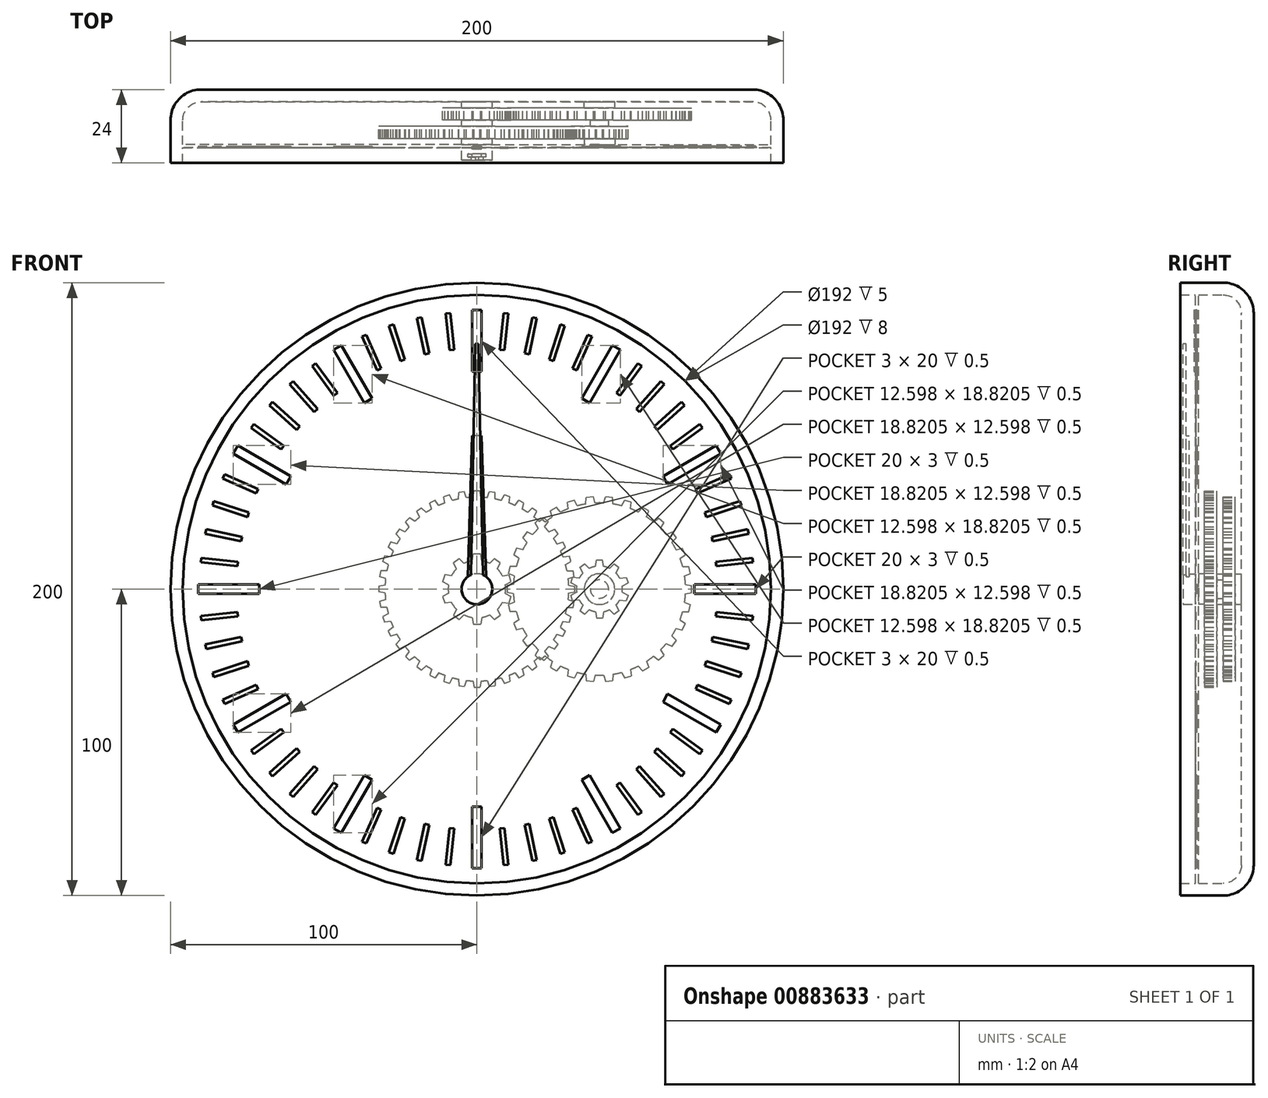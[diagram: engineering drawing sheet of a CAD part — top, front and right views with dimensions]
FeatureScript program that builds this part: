
annotation { "Feature Type Name" : "Feature", "Feature Type Description" : "" }
export const myFeature = defineFeature(function(context is Context, id is Id, definition is map)
    precondition{}
    {
        {
            var Q0;
            Q0=qCreatedBy(makeId("Front.planeOp"),FACE);
            var sketch = newSketch(context, id + "F0", { "sketchPlane" : qUnion([Q0])});
            skCircle(sketch, "E0", {"center": v(0, 0) * mm, "radius": 100 * mm});
            skSolve(sketch);
        }
        {
            var Q0;
            Q0 = qSketchRegion(id + "F0", true);
            extrude(context, id + "F1", {"entities" : qUnion([Q0]), "depth" : 24 * mm, "offsetDistance" : 25 * mm});
        }
        {
            var Q0;
            Q0=makeQuery(id+"F1.opExtrude","CAP_EDGE",EDGE,{"disambiguationData":[OSD([sQuery(id+"F0.wireOp",EDGE,"E0")])],"isStart":true});
            fillet(context, id + "F2", {"entities" : qUnion([Q0]), "radius" : 10 * mm, "tangentPropagation" : true, "allowEdgeOverflow" : false});
        }
        {
            var Q0;
            Q0=makeQuery(id+"F1.opExtrude","CAP_FACE",FACE,{"disambiguationData":[OSD([sQuery(id+"F0.wireOp",EDGE,"E0")])],"isStart":false});
            shell(context, id + "F3", {"entities" : qUnion([Q0]), "thickness" : 4 * mm});
        }
        {
            var Q0;
            {var subQ0=sQuery(id+"F0.wireOp",EDGE,"E0");Q0=makeQuery(id+"F3.opShell","OFFSET_FACE",FACE,{"disambiguationData":[OSD([subQ0]),TDD([makeQuery(id+"F1.opExtrude","CAP_FACE",FACE,{"disambiguationData":[OSD([subQ0])],"isStart":true})])]});}
            var sketch = newSketch(context, id + "F4", { "sketchPlane" : qUnion([Q0])});
            skCircle(sketch, "E1", {"center": v(0, 0) * mm, "radius": 3 * mm});
            skCircle(sketch, "E2", {"center": v(0, 0) * mm, "radius": 5 * mm});
            skCircle(sketch, "E3", {"center": v(40, 0) * mm, "radius": 3 * mm});
            skCircle(sketch, "E4", {"center": v(40, 0) * mm, "radius": 5 * mm});
            skSolve(sketch);
        }
        {
            var Q0;
            Q0 = qSketchRegion(id + "F4", true);
            extrude(context, id + "F5", {"entities" : qUnion([Q0]), "operationType" : NewBodyOperationType.ADD, "depth" : 2 * mm, "offsetDistance" : 25 * mm});
        }
        {
            var Q0;
            {var subQ0=sQuery(id+"F0.wireOp",EDGE,"E0");Q0=makeQuery(id+"F5.boolean.opBoolean","SPLIT",FACE,{"disambiguationData":[TD([makeQuery(id+"F5.opExtrude","SWEPT_FACE",FACE,{"disambiguationData":[OSD([sQuery(id+"F4.wireOp",EDGE,"E1")])]})])],"derivedFrom":makeQuery(id+"F3.opShell","OFFSET_FACE",FACE,{"disambiguationData":[OSD([subQ0]),TDD([makeQuery(id+"F1.opExtrude","CAP_FACE",FACE,{"disambiguationData":[OSD([subQ0])],"isStart":true})])]})});}
            extrude(context, id + "F6", {"entities" : qUnion([Q0]), "depth" : 19 * mm, "offsetDistance" : 25 * mm});
        }
        {
            var Q0;
            {var subQ0=sQuery(id+"F0.wireOp",EDGE,"E0");Q0=makeQuery(id+"F5.boolean.opBoolean","SPLIT",FACE,{"disambiguationData":[TD([makeQuery(id+"F5.opExtrude","SWEPT_FACE",FACE,{"disambiguationData":[OSD([sQuery(id+"F4.wireOp",EDGE,"E3")])]})])],"derivedFrom":makeQuery(id+"F3.opShell","OFFSET_FACE",FACE,{"disambiguationData":[OSD([subQ0]),TDD([makeQuery(id+"F1.opExtrude","CAP_FACE",FACE,{"disambiguationData":[OSD([subQ0])],"isStart":true})])]})});}
            extrude(context, id + "F7", {"entities" : qUnion([Q0]), "depth" : 8 * mm, "offsetDistance" : 25 * mm});
        }
        {
            var Q0;
            Q0=makeQuery(id+"F5.opExtrude","CAP_FACE",FACE,{"disambiguationData":[OSD([sQuery(id+"F4.wireOp",EDGE,"E1"),sQuery(id+"F4.wireOp",EDGE,"E2")])],"isStart":false});
            var sketch = newSketch(context, id + "F8", { "sketchPlane" : qUnion([Q0])});
            skCircle(sketch, "E5", {"center": v(0, 0) * mm, "radius": 9.38 * mm});
            skLineSegment(sketch, "E6", {"start": v(1.55, 9.25) * mm, "end": v(1.18, 11.38) * mm});
            skLineSegment(sketch, "E7", {"start": v(1.18, 11.38) * mm, "end": v(0, 11.38) * mm});
            skLineSegment(sketch, "E8.MirrorCS", {"start": v(-1.55, 9.25) * mm, "end": v(-1.18, 11.38) * mm});
            skLineSegment(sketch, "E9.MirrorCS", {"start": v(-1.18, 11.38) * mm, "end": v(0, 11.38) * mm});
            skLineSegment(sketch, "E10.1.0", {"start": v(-6.7, 6.57) * mm, "end": v(-7.64, 8.51) * mm});
            skLineSegment(sketch, "E10.1.1", {"start": v(-7.64, 8.51) * mm, "end": v(-6.69, 9.2) * mm});
            skLineSegment(sketch, "E10.1.2", {"start": v(-5.73, 9.9) * mm, "end": v(-6.69, 9.2) * mm});
            skLineSegment(sketch, "E10.1.3", {"start": v(-4.18, 8.4) * mm, "end": v(-5.73, 9.9) * mm});
            skLineSegment(sketch, "E10.2.0", {"start": v(-9.27, 1.38) * mm, "end": v(-11.18, 2.4) * mm});
            skLineSegment(sketch, "E10.2.1", {"start": v(-11.18, 2.4) * mm, "end": v(-10.82, 3.52) * mm});
            skLineSegment(sketch, "E10.2.2", {"start": v(-10.45, 4.64) * mm, "end": v(-10.82, 3.52) * mm});
            skLineSegment(sketch, "E10.2.3", {"start": v(-8.31, 4.33) * mm, "end": v(-10.45, 4.64) * mm});
            skLineSegment(sketch, "E11.1.3.0", {"start": v(-8.31, -4.33) * mm, "end": v(-10.45, -4.64) * mm});
            skLineSegment(sketch, "E11.3.3.0", {"start": v(-10.45, -4.64) * mm, "end": v(-10.82, -3.52) * mm});
            skLineSegment(sketch, "E11.6.3.0", {"start": v(-11.18, -2.4) * mm, "end": v(-10.82, -3.52) * mm});
            skLineSegment(sketch, "E11.9.3.0", {"start": v(-9.27, -1.38) * mm, "end": v(-11.18, -2.4) * mm});
            skLineSegment(sketch, "E11.1.4.0", {"start": v(-4.18, -8.4) * mm, "end": v(-5.73, -9.9) * mm});
            skLineSegment(sketch, "E11.3.4.0", {"start": v(-5.73, -9.9) * mm, "end": v(-6.69, -9.2) * mm});
            skLineSegment(sketch, "E11.6.4.0", {"start": v(-7.64, -8.51) * mm, "end": v(-6.69, -9.2) * mm});
            skLineSegment(sketch, "E11.9.4.0", {"start": v(-6.7, -6.57) * mm, "end": v(-7.64, -8.51) * mm});
            skLineSegment(sketch, "E11.1.5.0", {"start": v(1.55, -9.25) * mm, "end": v(1.18, -11.38) * mm});
            skLineSegment(sketch, "E11.3.5.0", {"start": v(1.18, -11.38) * mm, "end": v(0, -11.38) * mm});
            skLineSegment(sketch, "E11.6.5.0", {"start": v(-1.18, -11.38) * mm, "end": v(0, -11.38) * mm});
            skLineSegment(sketch, "E11.9.5.0", {"start": v(-1.55, -9.25) * mm, "end": v(-1.18, -11.38) * mm});
            skLineSegment(sketch, "E11.1.6.0", {"start": v(6.7, -6.57) * mm, "end": v(7.64, -8.51) * mm});
            skLineSegment(sketch, "E11.3.6.0", {"start": v(7.64, -8.51) * mm, "end": v(6.69, -9.2) * mm});
            skLineSegment(sketch, "E11.6.6.0", {"start": v(5.73, -9.9) * mm, "end": v(6.69, -9.2) * mm});
            skLineSegment(sketch, "E11.9.6.0", {"start": v(4.18, -8.4) * mm, "end": v(5.73, -9.9) * mm});
            skLineSegment(sketch, "E11.1.7.0", {"start": v(9.27, -1.38) * mm, "end": v(11.18, -2.4) * mm});
            skLineSegment(sketch, "E11.3.7.0", {"start": v(11.18, -2.4) * mm, "end": v(10.82, -3.52) * mm});
            skLineSegment(sketch, "E11.6.7.0", {"start": v(10.45, -4.64) * mm, "end": v(10.82, -3.52) * mm});
            skLineSegment(sketch, "E11.9.7.0", {"start": v(8.31, -4.33) * mm, "end": v(10.45, -4.64) * mm});
            skLineSegment(sketch, "E11.1.8.0", {"start": v(8.31, 4.33) * mm, "end": v(10.45, 4.64) * mm});
            skLineSegment(sketch, "E11.3.8.0", {"start": v(10.45, 4.64) * mm, "end": v(10.82, 3.52) * mm});
            skLineSegment(sketch, "E11.6.8.0", {"start": v(11.18, 2.4) * mm, "end": v(10.82, 3.52) * mm});
            skLineSegment(sketch, "E11.9.8.0", {"start": v(9.27, 1.38) * mm, "end": v(11.18, 2.4) * mm});
            skLineSegment(sketch, "E11.1.9.0", {"start": v(4.18, 8.4) * mm, "end": v(5.73, 9.9) * mm});
            skLineSegment(sketch, "E11.3.9.0", {"start": v(5.73, 9.9) * mm, "end": v(6.69, 9.2) * mm});
            skLineSegment(sketch, "E11.6.9.0", {"start": v(7.64, 8.51) * mm, "end": v(6.69, 9.2) * mm});
            skLineSegment(sketch, "E11.9.9.0", {"start": v(6.7, 6.57) * mm, "end": v(7.64, 8.51) * mm});
            skSolve(sketch);
        }
        {
            var Q0;
            Q0 = qSketchRegion(id + "F8", true);
            extrude(context, id + "F9", {"entities" : qUnion([Q0]), "operationType" : NewBodyOperationType.ADD, "depth" : 4 * mm, "offsetDistance" : 25 * mm});
        }
        {
            var Q0;
            Q0=makeQuery(id+"F5.opExtrude","CAP_FACE",FACE,{"disambiguationData":[OSD([sQuery(id+"F4.wireOp",EDGE,"E3"),sQuery(id+"F4.wireOp",EDGE,"E4")])],"isStart":false});
            var sketch = newSketch(context, id + "F10", { "sketchPlane" : qUnion([Q0])});
            skCircle(sketch, "E12", {"center": v(40, 0) * mm, "radius": 28.12 * mm});
            skLineSegment(sketch, "E13", {"start": v(11.92, 1.54) * mm, "end": v(9.88, 1.18) * mm});
            skLineSegment(sketch, "E14", {"start": v(9.88, 1.18) * mm, "end": v(9.88, 0) * mm});
            skLineSegment(sketch, "E15.MirrorCS", {"start": v(11.92, -1.54) * mm, "end": v(9.88, -1.18) * mm});
            skLineSegment(sketch, "E16.MirrorCS", {"start": v(9.88, -1.18) * mm, "end": v(9.88, 0) * mm});
            skLineSegment(sketch, "E17.1.0", {"start": v(12.21, -4.33) * mm, "end": v(10.29, -5.11) * mm});
            skLineSegment(sketch, "E17.1.1", {"start": v(10.29, -5.11) * mm, "end": v(10.53, -6.26) * mm});
            skLineSegment(sketch, "E17.1.2", {"start": v(10.78, -7.42) * mm, "end": v(10.53, -6.26) * mm});
            skLineSegment(sketch, "E17.1.3", {"start": v(12.85, -7.34) * mm, "end": v(10.78, -7.42) * mm});
            skLineSegment(sketch, "E17.2.0", {"start": v(13.72, -10.02) * mm, "end": v(12, -11.18) * mm});
            skLineSegment(sketch, "E17.2.1", {"start": v(12, -11.18) * mm, "end": v(12.48, -12.25) * mm});
            skLineSegment(sketch, "E17.2.2", {"start": v(12.96, -13.33) * mm, "end": v(12.48, -12.25) * mm});
            skLineSegment(sketch, "E17.2.3", {"start": v(14.97, -12.83) * mm, "end": v(12.96, -13.33) * mm});
            skLineSegment(sketch, "E18.2.3.0", {"start": v(16.38, -15.26) * mm, "end": v(14.94, -16.75) * mm});
            skLineSegment(sketch, "E18.3.3.0", {"start": v(14.94, -16.75) * mm, "end": v(15.63, -17.7) * mm});
            skLineSegment(sketch, "E18.6.3.0", {"start": v(16.32, -18.66) * mm, "end": v(15.63, -17.7) * mm});
            skLineSegment(sketch, "E18.9.3.0", {"start": v(18.18, -17.75) * mm, "end": v(16.32, -18.66) * mm});
            skLineSegment(sketch, "E18.2.4.0", {"start": v(20.07, -19.84) * mm, "end": v(18.97, -21.6) * mm});
            skLineSegment(sketch, "E18.3.4.0", {"start": v(18.97, -21.6) * mm, "end": v(19.84, -22.39) * mm});
            skLineSegment(sketch, "E18.6.4.0", {"start": v(20.72, -23.18) * mm, "end": v(19.84, -22.39) * mm});
            skLineSegment(sketch, "E18.9.4.0", {"start": v(22.35, -21.9) * mm, "end": v(20.72, -23.18) * mm});
            skLineSegment(sketch, "E18.2.5.0", {"start": v(24.63, -23.55) * mm, "end": v(23.92, -25.5) * mm});
            skLineSegment(sketch, "E18.3.5.0", {"start": v(23.92, -25.5) * mm, "end": v(24.94, -26.09) * mm});
            skLineSegment(sketch, "E18.6.5.0", {"start": v(25.96, -26.68) * mm, "end": v(24.94, -26.09) * mm});
            skLineSegment(sketch, "E18.9.5.0", {"start": v(27.3, -25.09) * mm, "end": v(25.96, -26.68) * mm});
            skLineSegment(sketch, "E18.2.6.0", {"start": v(29.86, -26.23) * mm, "end": v(29.57, -28.29) * mm});
            skLineSegment(sketch, "E18.3.6.0", {"start": v(29.57, -28.29) * mm, "end": v(30.7, -28.65) * mm});
            skLineSegment(sketch, "E18.6.6.0", {"start": v(31.81, -29.01) * mm, "end": v(30.7, -28.65) * mm});
            skLineSegment(sketch, "E18.9.6.0", {"start": v(32.78, -27.18) * mm, "end": v(31.81, -29.01) * mm});
            skLineSegment(sketch, "E18.2.7.0", {"start": v(35.53, -27.77) * mm, "end": v(35.68, -29.84) * mm});
            skLineSegment(sketch, "E18.3.7.0", {"start": v(35.68, -29.84) * mm, "end": v(36.85, -29.96) * mm});
            skLineSegment(sketch, "E18.6.7.0", {"start": v(38.02, -30.08) * mm, "end": v(36.85, -29.96) * mm});
            skLineSegment(sketch, "E18.9.7.0", {"start": v(38.6, -28.09) * mm, "end": v(38.02, -30.08) * mm});
            skLineSegment(sketch, "E18.2.8.0", {"start": v(41.4, -28.09) * mm, "end": v(41.98, -30.08) * mm});
            skLineSegment(sketch, "E18.3.8.0", {"start": v(41.98, -30.08) * mm, "end": v(43.15, -29.96) * mm});
            skLineSegment(sketch, "E18.6.8.0", {"start": v(44.32, -29.84) * mm, "end": v(43.15, -29.96) * mm});
            skLineSegment(sketch, "E18.9.8.0", {"start": v(44.47, -27.77) * mm, "end": v(44.32, -29.84) * mm});
            skLineSegment(sketch, "E18.2.9.0", {"start": v(47.22, -27.18) * mm, "end": v(48.19, -29.01) * mm});
            skLineSegment(sketch, "E18.3.9.0", {"start": v(48.19, -29.01) * mm, "end": v(49.3, -28.65) * mm});
            skLineSegment(sketch, "E18.6.9.0", {"start": v(50.43, -28.29) * mm, "end": v(49.3, -28.65) * mm});
            skLineSegment(sketch, "E18.9.9.0", {"start": v(50.14, -26.23) * mm, "end": v(50.43, -28.29) * mm});
            skLineSegment(sketch, "E18.2.10.0", {"start": v(52.7, -25.09) * mm, "end": v(54.04, -26.68) * mm});
            skLineSegment(sketch, "E18.3.10.0", {"start": v(54.04, -26.68) * mm, "end": v(55.06, -26.09) * mm});
            skLineSegment(sketch, "E18.6.10.0", {"start": v(56.08, -25.5) * mm, "end": v(55.06, -26.09) * mm});
            skLineSegment(sketch, "E18.9.10.0", {"start": v(55.37, -23.55) * mm, "end": v(56.08, -25.5) * mm});
            skLineSegment(sketch, "E18.2.11.0", {"start": v(57.65, -21.9) * mm, "end": v(59.28, -23.18) * mm});
            skLineSegment(sketch, "E18.3.11.0", {"start": v(59.28, -23.18) * mm, "end": v(60.16, -22.39) * mm});
            skLineSegment(sketch, "E18.6.11.0", {"start": v(61.03, -21.6) * mm, "end": v(60.16, -22.39) * mm});
            skLineSegment(sketch, "E18.9.11.0", {"start": v(59.93, -19.84) * mm, "end": v(61.03, -21.6) * mm});
            skLineSegment(sketch, "E18.2.12.0", {"start": v(61.82, -17.75) * mm, "end": v(63.68, -18.66) * mm});
            skLineSegment(sketch, "E18.3.12.0", {"start": v(63.68, -18.66) * mm, "end": v(64.37, -17.7) * mm});
            skLineSegment(sketch, "E18.6.12.0", {"start": v(65.06, -16.75) * mm, "end": v(64.37, -17.7) * mm});
            skLineSegment(sketch, "E18.9.12.0", {"start": v(63.62, -15.26) * mm, "end": v(65.06, -16.75) * mm});
            skLineSegment(sketch, "E18.2.13.0", {"start": v(65.03, -12.83) * mm, "end": v(67.04, -13.33) * mm});
            skLineSegment(sketch, "E18.3.13.0", {"start": v(67.04, -13.33) * mm, "end": v(67.52, -12.25) * mm});
            skLineSegment(sketch, "E18.6.13.0", {"start": v(68, -11.18) * mm, "end": v(67.52, -12.25) * mm});
            skLineSegment(sketch, "E18.9.13.0", {"start": v(66.28, -10.02) * mm, "end": v(68, -11.18) * mm});
            skLineSegment(sketch, "E18.2.14.0", {"start": v(67.15, -7.34) * mm, "end": v(69.22, -7.42) * mm});
            skLineSegment(sketch, "E18.3.14.0", {"start": v(69.22, -7.42) * mm, "end": v(69.47, -6.26) * mm});
            skLineSegment(sketch, "E18.6.14.0", {"start": v(69.71, -5.11) * mm, "end": v(69.47, -6.26) * mm});
            skLineSegment(sketch, "E18.9.14.0", {"start": v(67.79, -4.33) * mm, "end": v(69.71, -5.11) * mm});
            skLineSegment(sketch, "E18.2.15.0", {"start": v(68.08, -1.54) * mm, "end": v(70.13, -1.18) * mm});
            skLineSegment(sketch, "E18.3.15.0", {"start": v(70.12, -1.18) * mm, "end": v(70.12, 0) * mm});
            skLineSegment(sketch, "E18.6.15.0", {"start": v(70.12, 1.18) * mm, "end": v(70.12, 0) * mm});
            skLineSegment(sketch, "E18.9.15.0", {"start": v(68.08, 1.54) * mm, "end": v(70.13, 1.18) * mm});
            skLineSegment(sketch, "E18.2.16.0", {"start": v(67.79, 4.33) * mm, "end": v(69.71, 5.11) * mm});
            skLineSegment(sketch, "E18.3.16.0", {"start": v(69.71, 5.11) * mm, "end": v(69.47, 6.26) * mm});
            skLineSegment(sketch, "E18.6.16.0", {"start": v(69.22, 7.42) * mm, "end": v(69.47, 6.26) * mm});
            skLineSegment(sketch, "E18.9.16.0", {"start": v(67.15, 7.34) * mm, "end": v(69.22, 7.42) * mm});
            skLineSegment(sketch, "E18.2.17.0", {"start": v(66.28, 10.02) * mm, "end": v(68, 11.18) * mm});
            skLineSegment(sketch, "E18.3.17.0", {"start": v(68, 11.18) * mm, "end": v(67.52, 12.25) * mm});
            skLineSegment(sketch, "E18.6.17.0", {"start": v(67.04, 13.33) * mm, "end": v(67.52, 12.25) * mm});
            skLineSegment(sketch, "E18.9.17.0", {"start": v(65.03, 12.83) * mm, "end": v(67.04, 13.33) * mm});
            skLineSegment(sketch, "E18.2.18.0", {"start": v(63.62, 15.26) * mm, "end": v(65.06, 16.75) * mm});
            skLineSegment(sketch, "E18.3.18.0", {"start": v(65.06, 16.75) * mm, "end": v(64.37, 17.7) * mm});
            skLineSegment(sketch, "E18.6.18.0", {"start": v(63.68, 18.66) * mm, "end": v(64.37, 17.7) * mm});
            skLineSegment(sketch, "E18.9.18.0", {"start": v(61.82, 17.75) * mm, "end": v(63.68, 18.66) * mm});
            skLineSegment(sketch, "E18.2.19.0", {"start": v(59.93, 19.84) * mm, "end": v(61.03, 21.6) * mm});
            skLineSegment(sketch, "E18.3.19.0", {"start": v(61.03, 21.6) * mm, "end": v(60.16, 22.39) * mm});
            skLineSegment(sketch, "E18.6.19.0", {"start": v(59.28, 23.18) * mm, "end": v(60.16, 22.39) * mm});
            skLineSegment(sketch, "E18.9.19.0", {"start": v(57.65, 21.9) * mm, "end": v(59.28, 23.18) * mm});
            skLineSegment(sketch, "E18.2.20.0", {"start": v(55.37, 23.55) * mm, "end": v(56.08, 25.5) * mm});
            skLineSegment(sketch, "E18.3.20.0", {"start": v(56.08, 25.5) * mm, "end": v(55.06, 26.09) * mm});
            skLineSegment(sketch, "E18.6.20.0", {"start": v(54.04, 26.68) * mm, "end": v(55.06, 26.09) * mm});
            skLineSegment(sketch, "E18.9.20.0", {"start": v(52.7, 25.09) * mm, "end": v(54.04, 26.68) * mm});
            skLineSegment(sketch, "E18.2.21.0", {"start": v(50.14, 26.23) * mm, "end": v(50.43, 28.29) * mm});
            skLineSegment(sketch, "E18.3.21.0", {"start": v(50.43, 28.29) * mm, "end": v(49.3, 28.65) * mm});
            skLineSegment(sketch, "E18.6.21.0", {"start": v(48.19, 29.01) * mm, "end": v(49.3, 28.65) * mm});
            skLineSegment(sketch, "E18.9.21.0", {"start": v(47.22, 27.18) * mm, "end": v(48.19, 29.01) * mm});
            skLineSegment(sketch, "E18.2.22.0", {"start": v(44.47, 27.77) * mm, "end": v(44.32, 29.84) * mm});
            skLineSegment(sketch, "E18.3.22.0", {"start": v(44.32, 29.84) * mm, "end": v(43.15, 29.96) * mm});
            skLineSegment(sketch, "E18.6.22.0", {"start": v(41.98, 30.08) * mm, "end": v(43.15, 29.96) * mm});
            skLineSegment(sketch, "E18.9.22.0", {"start": v(41.4, 28.09) * mm, "end": v(41.98, 30.08) * mm});
            skLineSegment(sketch, "E18.2.23.0", {"start": v(38.6, 28.09) * mm, "end": v(38.02, 30.08) * mm});
            skLineSegment(sketch, "E18.3.23.0", {"start": v(38.02, 30.08) * mm, "end": v(36.85, 29.96) * mm});
            skLineSegment(sketch, "E18.6.23.0", {"start": v(35.68, 29.84) * mm, "end": v(36.85, 29.96) * mm});
            skLineSegment(sketch, "E18.9.23.0", {"start": v(35.53, 27.77) * mm, "end": v(35.68, 29.84) * mm});
            skLineSegment(sketch, "E18.2.24.0", {"start": v(32.78, 27.18) * mm, "end": v(31.81, 29.01) * mm});
            skLineSegment(sketch, "E18.3.24.0", {"start": v(31.81, 29.01) * mm, "end": v(30.7, 28.65) * mm});
            skLineSegment(sketch, "E18.6.24.0", {"start": v(29.57, 28.29) * mm, "end": v(30.7, 28.65) * mm});
            skLineSegment(sketch, "E18.9.24.0", {"start": v(29.86, 26.23) * mm, "end": v(29.57, 28.29) * mm});
            skLineSegment(sketch, "E18.2.25.0", {"start": v(27.3, 25.09) * mm, "end": v(25.96, 26.68) * mm});
            skLineSegment(sketch, "E18.3.25.0", {"start": v(25.96, 26.68) * mm, "end": v(24.94, 26.09) * mm});
            skLineSegment(sketch, "E18.6.25.0", {"start": v(23.92, 25.5) * mm, "end": v(24.94, 26.09) * mm});
            skLineSegment(sketch, "E18.9.25.0", {"start": v(24.63, 23.55) * mm, "end": v(23.92, 25.5) * mm});
            skLineSegment(sketch, "E18.2.26.0", {"start": v(22.35, 21.9) * mm, "end": v(20.72, 23.18) * mm});
            skLineSegment(sketch, "E18.3.26.0", {"start": v(20.72, 23.18) * mm, "end": v(19.84, 22.39) * mm});
            skLineSegment(sketch, "E18.6.26.0", {"start": v(18.97, 21.6) * mm, "end": v(19.84, 22.39) * mm});
            skLineSegment(sketch, "E18.9.26.0", {"start": v(20.07, 19.84) * mm, "end": v(18.97, 21.6) * mm});
            skLineSegment(sketch, "E18.2.27.0", {"start": v(18.18, 17.75) * mm, "end": v(16.32, 18.66) * mm});
            skLineSegment(sketch, "E18.3.27.0", {"start": v(16.32, 18.66) * mm, "end": v(15.63, 17.7) * mm});
            skLineSegment(sketch, "E18.6.27.0", {"start": v(14.94, 16.75) * mm, "end": v(15.63, 17.7) * mm});
            skLineSegment(sketch, "E18.9.27.0", {"start": v(16.38, 15.26) * mm, "end": v(14.94, 16.75) * mm});
            skLineSegment(sketch, "E18.2.28.0", {"start": v(14.97, 12.83) * mm, "end": v(12.96, 13.33) * mm});
            skLineSegment(sketch, "E18.3.28.0", {"start": v(12.96, 13.33) * mm, "end": v(12.48, 12.25) * mm});
            skLineSegment(sketch, "E18.6.28.0", {"start": v(12, 11.18) * mm, "end": v(12.48, 12.25) * mm});
            skLineSegment(sketch, "E18.9.28.0", {"start": v(13.72, 10.02) * mm, "end": v(12, 11.18) * mm});
            skLineSegment(sketch, "E18.2.29.0", {"start": v(12.85, 7.34) * mm, "end": v(10.78, 7.42) * mm});
            skLineSegment(sketch, "E18.3.29.0", {"start": v(10.78, 7.42) * mm, "end": v(10.53, 6.26) * mm});
            skLineSegment(sketch, "E18.6.29.0", {"start": v(10.29, 5.11) * mm, "end": v(10.53, 6.26) * mm});
            skLineSegment(sketch, "E18.9.29.0", {"start": v(12.21, 4.33) * mm, "end": v(10.29, 5.11) * mm});
            skSolve(sketch);
        }
        {
            var Q0;
            Q0 = qSketchRegion(id + "F10", true);
            extrude(context, id + "F11", {"entities" : qUnion([Q0]), "operationType" : NewBodyOperationType.ADD, "depth" : 4 * mm, "offsetDistance" : 25 * mm});
        }
        {
            var Q0;
            Q0=makeQuery(id+"F9.opExtrude","CAP_FACE",FACE,{"disambiguationData":[OSD([sQuery(id+"F8.wireOp",EDGE,"E5"),sQuery(id+"F8.wireOp",EDGE,"E6"),sQuery(id+"F8.wireOp",EDGE,"E7"),sQuery(id+"F8.wireOp",EDGE,"E8.MirrorCS"),sQuery(id+"F8.wireOp",EDGE,"E9.MirrorCS"),sQuery(id+"F8.wireOp",EDGE,"E10.1.0"),sQuery(id+"F8.wireOp",EDGE,"E10.1.1"),sQuery(id+"F8.wireOp",EDGE,"E10.1.2"),sQuery(id+"F8.wireOp",EDGE,"E10.1.3"),sQuery(id+"F8.wireOp",EDGE,"E10.2.0"),sQuery(id+"F8.wireOp",EDGE,"E10.2.1"),sQuery(id+"F8.wireOp",EDGE,"E10.2.2"),sQuery(id+"F8.wireOp",EDGE,"E10.2.3"),sQuery(id+"F8.wireOp",EDGE,"E11.1.3.0"),sQuery(id+"F8.wireOp",EDGE,"E11.3.3.0"),sQuery(id+"F8.wireOp",EDGE,"E11.6.3.0"),sQuery(id+"F8.wireOp",EDGE,"E11.9.3.0"),sQuery(id+"F8.wireOp",EDGE,"E11.1.4.0"),sQuery(id+"F8.wireOp",EDGE,"E11.3.4.0"),sQuery(id+"F8.wireOp",EDGE,"E11.6.4.0"),sQuery(id+"F8.wireOp",EDGE,"E11.9.4.0"),sQuery(id+"F8.wireOp",EDGE,"E11.1.5.0"),sQuery(id+"F8.wireOp",EDGE,"E11.3.5.0"),sQuery(id+"F8.wireOp",EDGE,"E11.6.5.0"),sQuery(id+"F8.wireOp",EDGE,"E11.9.5.0"),sQuery(id+"F8.wireOp",EDGE,"E11.1.6.0"),sQuery(id+"F8.wireOp",EDGE,"E11.3.6.0"),sQuery(id+"F8.wireOp",EDGE,"E11.6.6.0"),sQuery(id+"F8.wireOp",EDGE,"E11.9.6.0"),sQuery(id+"F8.wireOp",EDGE,"E11.1.7.0"),sQuery(id+"F8.wireOp",EDGE,"E11.3.7.0"),sQuery(id+"F8.wireOp",EDGE,"E11.6.7.0"),sQuery(id+"F8.wireOp",EDGE,"E11.9.7.0"),sQuery(id+"F8.wireOp",EDGE,"E11.1.8.0"),sQuery(id+"F8.wireOp",EDGE,"E11.3.8.0"),sQuery(id+"F8.wireOp",EDGE,"E11.6.8.0"),sQuery(id+"F8.wireOp",EDGE,"E11.9.8.0"),sQuery(id+"F8.wireOp",EDGE,"E11.1.9.0"),sQuery(id+"F8.wireOp",EDGE,"E11.3.9.0"),sQuery(id+"F8.wireOp",EDGE,"E11.6.9.0"),sQuery(id+"F8.wireOp",EDGE,"E11.9.9.0")])],"isStart":false});
            var sketch = newSketch(context, id + "F12", { "sketchPlane" : qUnion([Q0])});
            skCircle(sketch, "E19.0", {"center": v(0, 0) * mm, "radius": 3 * mm});
            skCircle(sketch, "E20.0", {"center": v(0, 0) * mm, "radius": 5 * mm});
            skSolve(sketch);
        }
        {
            var Q0;
            Q0 = qSketchRegion(id + "F12", true);
            extrude(context, id + "F13", {"entities" : qUnion([Q0]), "depth" : 2 * mm, "offsetDistance" : 25 * mm});
        }
        {
            var Q0;
            Q0=makeQuery(id+"F13.opExtrude","CAP_FACE",FACE,{"disambiguationData":[OSD([sQuery(id+"F12.wireOp",EDGE,"E19.0"),sQuery(id+"F12.wireOp",EDGE,"E20.0")])],"isStart":false});
            var sketch = newSketch(context, id + "F14", { "sketchPlane" : qUnion([Q0])});
            skCircle(sketch, "E21.0", {"center": v(0, 0) * mm, "radius": 3 * mm});
            skCircle(sketch, "E22", {"center": v(0, 0) * mm, "radius": 30 * mm});
            skLineSegment(sketch, "E23", {"start": v(1.3, 29.97) * mm, "end": v(0.94, 32) * mm});
            skLineSegment(sketch, "E24", {"start": v(0.94, 32) * mm, "end": v(0, 32) * mm});
            skLineSegment(sketch, "E25.MirrorCS", {"start": v(-0.94, 32) * mm, "end": v(0, 32) * mm});
            skLineSegment(sketch, "E26.MirrorCS", {"start": v(-1.3, 29.97) * mm, "end": v(-0.94, 32) * mm});
            skLineSegment(sketch, "E27.1.0", {"start": v(-4.08, 31.75) * mm, "end": v(-5, 31.6) * mm});
            skLineSegment(sketch, "E27.1.1", {"start": v(-5.94, 31.46) * mm, "end": v(-5, 31.6) * mm});
            skLineSegment(sketch, "E27.1.2", {"start": v(-5.97, 29.4) * mm, "end": v(-5.94, 31.46) * mm});
            skLineSegment(sketch, "E27.1.3", {"start": v(-3.4, 29.8) * mm, "end": v(-4.08, 31.75) * mm});
            skLineSegment(sketch, "E27.2.0", {"start": v(-9, 30.73) * mm, "end": v(-9.89, 30.43) * mm});
            skLineSegment(sketch, "E27.2.1", {"start": v(-10.78, 30.14) * mm, "end": v(-9.89, 30.43) * mm});
            skLineSegment(sketch, "E27.2.2", {"start": v(-10.5, 28.1) * mm, "end": v(-10.78, 30.14) * mm});
            skLineSegment(sketch, "E27.2.3", {"start": v(-8.03, 28.9) * mm, "end": v(-9, 30.73) * mm});
            skLineSegment(sketch, "E27.3.0", {"start": v(-13.69, 28.94) * mm, "end": v(-14.53, 28.51) * mm});
            skLineSegment(sketch, "E27.3.1", {"start": v(-15.37, 28.08) * mm, "end": v(-14.53, 28.51) * mm});
            skLineSegment(sketch, "E27.3.2", {"start": v(-14.77, 26.11) * mm, "end": v(-15.37, 28.08) * mm});
            skLineSegment(sketch, "E27.3.3", {"start": v(-12.45, 27.3) * mm, "end": v(-13.69, 28.94) * mm});
            skLineSegment(sketch, "E27.4.0", {"start": v(-18.05, 26.44) * mm, "end": v(-18.8, 25.89) * mm});
            skLineSegment(sketch, "E27.4.1", {"start": v(-19.57, 25.33) * mm, "end": v(-18.8, 25.89) * mm});
            skLineSegment(sketch, "E27.4.2", {"start": v(-18.67, 23.48) * mm, "end": v(-19.57, 25.33) * mm});
            skLineSegment(sketch, "E27.4.3", {"start": v(-16.57, 25.01) * mm, "end": v(-18.05, 26.44) * mm});
            skLineSegment(sketch, "E27.5.0", {"start": v(-21.96, 23.3) * mm, "end": v(-22.63, 22.63) * mm});
            skLineSegment(sketch, "E27.5.1", {"start": v(-23.3, 21.96) * mm, "end": v(-22.63, 22.63) * mm});
            skLineSegment(sketch, "E27.5.2", {"start": v(-22.11, 20.27) * mm, "end": v(-23.3, 21.96) * mm});
            skLineSegment(sketch, "E27.5.3", {"start": v(-20.27, 22.11) * mm, "end": v(-21.96, 23.3) * mm});
            skLineSegment(sketch, "E27.6.0", {"start": v(-25.33, 19.57) * mm, "end": v(-25.89, 18.8) * mm});
            skLineSegment(sketch, "E27.6.1", {"start": v(-26.44, 18.05) * mm, "end": v(-25.89, 18.8) * mm});
            skLineSegment(sketch, "E27.6.2", {"start": v(-25.01, 16.57) * mm, "end": v(-26.44, 18.05) * mm});
            skLineSegment(sketch, "E27.6.3", {"start": v(-23.48, 18.67) * mm, "end": v(-25.33, 19.57) * mm});
            skLineSegment(sketch, "E27.7.0", {"start": v(-28.08, 15.37) * mm, "end": v(-28.51, 14.53) * mm});
            skLineSegment(sketch, "E27.7.1", {"start": v(-28.94, 13.69) * mm, "end": v(-28.51, 14.53) * mm});
            skLineSegment(sketch, "E27.7.2", {"start": v(-27.3, 12.45) * mm, "end": v(-28.94, 13.69) * mm});
            skLineSegment(sketch, "E27.7.3", {"start": v(-26.11, 14.77) * mm, "end": v(-28.08, 15.37) * mm});
            skLineSegment(sketch, "E27.8.0", {"start": v(-30.14, 10.78) * mm, "end": v(-30.43, 9.89) * mm});
            skLineSegment(sketch, "E27.8.1", {"start": v(-30.73, 9) * mm, "end": v(-30.43, 9.89) * mm});
            skLineSegment(sketch, "E27.8.2", {"start": v(-28.9, 8.03) * mm, "end": v(-30.73, 9) * mm});
            skLineSegment(sketch, "E27.8.3", {"start": v(-28.1, 10.5) * mm, "end": v(-30.14, 10.78) * mm});
            skLineSegment(sketch, "E27.9.0", {"start": v(-31.46, 5.94) * mm, "end": v(-31.6, 5) * mm});
            skLineSegment(sketch, "E27.9.1", {"start": v(-31.75, 4.08) * mm, "end": v(-31.6, 5) * mm});
            skLineSegment(sketch, "E27.9.2", {"start": v(-29.8, 3.4) * mm, "end": v(-31.75, 4.08) * mm});
            skLineSegment(sketch, "E27.9.3", {"start": v(-29.4, 5.97) * mm, "end": v(-31.46, 5.94) * mm});
            skLineSegment(sketch, "E27.10.0", {"start": v(-32, 0.94) * mm, "end": v(-32, 0) * mm});
            skLineSegment(sketch, "E27.10.1", {"start": v(-32, -0.94) * mm, "end": v(-32, 0) * mm});
            skLineSegment(sketch, "E27.10.2", {"start": v(-29.97, -1.3) * mm, "end": v(-32, -0.94) * mm});
            skLineSegment(sketch, "E27.10.3", {"start": v(-29.97, 1.3) * mm, "end": v(-32, 0.94) * mm});
            skLineSegment(sketch, "E27.11.0", {"start": v(-31.75, -4.08) * mm, "end": v(-31.6, -5) * mm});
            skLineSegment(sketch, "E27.11.1", {"start": v(-31.46, -5.94) * mm, "end": v(-31.6, -5) * mm});
            skLineSegment(sketch, "E27.11.2", {"start": v(-29.4, -5.97) * mm, "end": v(-31.46, -5.94) * mm});
            skLineSegment(sketch, "E27.11.3", {"start": v(-29.8, -3.4) * mm, "end": v(-31.75, -4.08) * mm});
            skLineSegment(sketch, "E27.12.0", {"start": v(-30.73, -9) * mm, "end": v(-30.43, -9.89) * mm});
            skLineSegment(sketch, "E27.12.1", {"start": v(-30.14, -10.78) * mm, "end": v(-30.43, -9.89) * mm});
            skLineSegment(sketch, "E27.12.2", {"start": v(-28.1, -10.5) * mm, "end": v(-30.14, -10.78) * mm});
            skLineSegment(sketch, "E27.12.3", {"start": v(-28.9, -8.03) * mm, "end": v(-30.73, -9) * mm});
            skLineSegment(sketch, "E27.13.0", {"start": v(-28.94, -13.69) * mm, "end": v(-28.51, -14.53) * mm});
            skLineSegment(sketch, "E27.13.1", {"start": v(-28.08, -15.37) * mm, "end": v(-28.51, -14.53) * mm});
            skLineSegment(sketch, "E27.13.2", {"start": v(-26.11, -14.77) * mm, "end": v(-28.08, -15.37) * mm});
            skLineSegment(sketch, "E27.13.3", {"start": v(-27.3, -12.45) * mm, "end": v(-28.94, -13.69) * mm});
            skLineSegment(sketch, "E27.14.0", {"start": v(-26.44, -18.05) * mm, "end": v(-25.89, -18.8) * mm});
            skLineSegment(sketch, "E27.14.1", {"start": v(-25.33, -19.57) * mm, "end": v(-25.89, -18.8) * mm});
            skLineSegment(sketch, "E27.14.2", {"start": v(-23.48, -18.67) * mm, "end": v(-25.33, -19.57) * mm});
            skLineSegment(sketch, "E27.14.3", {"start": v(-25.01, -16.57) * mm, "end": v(-26.44, -18.05) * mm});
            skLineSegment(sketch, "E27.15.0", {"start": v(-23.3, -21.96) * mm, "end": v(-22.63, -22.63) * mm});
            skLineSegment(sketch, "E27.15.1", {"start": v(-21.96, -23.3) * mm, "end": v(-22.63, -22.63) * mm});
            skLineSegment(sketch, "E27.15.2", {"start": v(-20.27, -22.11) * mm, "end": v(-21.96, -23.3) * mm});
            skLineSegment(sketch, "E27.15.3", {"start": v(-22.11, -20.27) * mm, "end": v(-23.3, -21.96) * mm});
            skLineSegment(sketch, "E27.16.0", {"start": v(-19.57, -25.33) * mm, "end": v(-18.8, -25.89) * mm});
            skLineSegment(sketch, "E27.16.1", {"start": v(-18.05, -26.44) * mm, "end": v(-18.8, -25.89) * mm});
            skLineSegment(sketch, "E27.16.2", {"start": v(-16.57, -25.01) * mm, "end": v(-18.05, -26.44) * mm});
            skLineSegment(sketch, "E27.16.3", {"start": v(-18.67, -23.48) * mm, "end": v(-19.57, -25.33) * mm});
            skLineSegment(sketch, "E27.17.0", {"start": v(-15.37, -28.08) * mm, "end": v(-14.53, -28.51) * mm});
            skLineSegment(sketch, "E27.17.1", {"start": v(-13.69, -28.94) * mm, "end": v(-14.53, -28.51) * mm});
            skLineSegment(sketch, "E27.17.2", {"start": v(-12.45, -27.3) * mm, "end": v(-13.69, -28.94) * mm});
            skLineSegment(sketch, "E27.17.3", {"start": v(-14.77, -26.11) * mm, "end": v(-15.37, -28.08) * mm});
            skLineSegment(sketch, "E27.18.0", {"start": v(-10.78, -30.14) * mm, "end": v(-9.89, -30.43) * mm});
            skLineSegment(sketch, "E27.18.1", {"start": v(-9, -30.73) * mm, "end": v(-9.89, -30.43) * mm});
            skLineSegment(sketch, "E27.18.2", {"start": v(-8.03, -28.9) * mm, "end": v(-9, -30.73) * mm});
            skLineSegment(sketch, "E27.18.3", {"start": v(-10.5, -28.1) * mm, "end": v(-10.78, -30.14) * mm});
            skLineSegment(sketch, "E27.19.0", {"start": v(-5.94, -31.46) * mm, "end": v(-5, -31.6) * mm});
            skLineSegment(sketch, "E27.19.1", {"start": v(-4.08, -31.75) * mm, "end": v(-5, -31.6) * mm});
            skLineSegment(sketch, "E27.19.2", {"start": v(-3.4, -29.8) * mm, "end": v(-4.08, -31.75) * mm});
            skLineSegment(sketch, "E27.19.3", {"start": v(-5.97, -29.4) * mm, "end": v(-5.94, -31.46) * mm});
            skLineSegment(sketch, "E27.20.0", {"start": v(-0.94, -32) * mm, "end": v(0, -32) * mm});
            skLineSegment(sketch, "E27.20.1", {"start": v(0.94, -32) * mm, "end": v(0, -32) * mm});
            skLineSegment(sketch, "E27.20.2", {"start": v(1.3, -29.97) * mm, "end": v(0.94, -32) * mm});
            skLineSegment(sketch, "E27.20.3", {"start": v(-1.3, -29.97) * mm, "end": v(-0.94, -32) * mm});
            skLineSegment(sketch, "E27.21.0", {"start": v(4.08, -31.75) * mm, "end": v(5, -31.6) * mm});
            skLineSegment(sketch, "E27.21.1", {"start": v(5.94, -31.46) * mm, "end": v(5, -31.6) * mm});
            skLineSegment(sketch, "E27.21.2", {"start": v(5.97, -29.4) * mm, "end": v(5.94, -31.46) * mm});
            skLineSegment(sketch, "E27.21.3", {"start": v(3.4, -29.8) * mm, "end": v(4.08, -31.75) * mm});
            skLineSegment(sketch, "E27.22.0", {"start": v(9, -30.73) * mm, "end": v(9.89, -30.43) * mm});
            skLineSegment(sketch, "E27.22.1", {"start": v(10.78, -30.14) * mm, "end": v(9.89, -30.43) * mm});
            skLineSegment(sketch, "E27.22.2", {"start": v(10.5, -28.1) * mm, "end": v(10.78, -30.14) * mm});
            skLineSegment(sketch, "E27.22.3", {"start": v(8.03, -28.9) * mm, "end": v(9, -30.73) * mm});
            skLineSegment(sketch, "E27.23.0", {"start": v(13.69, -28.94) * mm, "end": v(14.53, -28.51) * mm});
            skLineSegment(sketch, "E27.23.1", {"start": v(15.37, -28.08) * mm, "end": v(14.53, -28.51) * mm});
            skLineSegment(sketch, "E27.23.2", {"start": v(14.77, -26.11) * mm, "end": v(15.37, -28.08) * mm});
            skLineSegment(sketch, "E27.23.3", {"start": v(12.45, -27.3) * mm, "end": v(13.69, -28.94) * mm});
            skLineSegment(sketch, "E27.24.0", {"start": v(18.05, -26.44) * mm, "end": v(18.8, -25.89) * mm});
            skLineSegment(sketch, "E27.24.1", {"start": v(19.57, -25.33) * mm, "end": v(18.8, -25.89) * mm});
            skLineSegment(sketch, "E27.24.2", {"start": v(18.67, -23.48) * mm, "end": v(19.57, -25.33) * mm});
            skLineSegment(sketch, "E27.24.3", {"start": v(16.57, -25.01) * mm, "end": v(18.05, -26.44) * mm});
            skLineSegment(sketch, "E27.25.0", {"start": v(21.96, -23.3) * mm, "end": v(22.63, -22.63) * mm});
            skLineSegment(sketch, "E27.25.1", {"start": v(23.3, -21.96) * mm, "end": v(22.63, -22.63) * mm});
            skLineSegment(sketch, "E27.25.2", {"start": v(22.11, -20.27) * mm, "end": v(23.3, -21.96) * mm});
            skLineSegment(sketch, "E27.25.3", {"start": v(20.27, -22.11) * mm, "end": v(21.96, -23.3) * mm});
            skLineSegment(sketch, "E27.26.0", {"start": v(25.33, -19.57) * mm, "end": v(25.89, -18.8) * mm});
            skLineSegment(sketch, "E27.26.1", {"start": v(26.44, -18.05) * mm, "end": v(25.89, -18.8) * mm});
            skLineSegment(sketch, "E27.26.2", {"start": v(25.01, -16.57) * mm, "end": v(26.44, -18.05) * mm});
            skLineSegment(sketch, "E27.26.3", {"start": v(23.48, -18.67) * mm, "end": v(25.33, -19.57) * mm});
            skLineSegment(sketch, "E27.27.0", {"start": v(28.08, -15.37) * mm, "end": v(28.51, -14.53) * mm});
            skLineSegment(sketch, "E27.27.1", {"start": v(28.94, -13.69) * mm, "end": v(28.51, -14.53) * mm});
            skLineSegment(sketch, "E27.27.2", {"start": v(27.3, -12.45) * mm, "end": v(28.94, -13.69) * mm});
            skLineSegment(sketch, "E27.27.3", {"start": v(26.11, -14.77) * mm, "end": v(28.08, -15.37) * mm});
            skLineSegment(sketch, "E27.28.0", {"start": v(30.14, -10.78) * mm, "end": v(30.43, -9.89) * mm});
            skLineSegment(sketch, "E27.28.1", {"start": v(30.73, -9) * mm, "end": v(30.43, -9.89) * mm});
            skLineSegment(sketch, "E27.28.2", {"start": v(28.9, -8.03) * mm, "end": v(30.73, -9) * mm});
            skLineSegment(sketch, "E27.28.3", {"start": v(28.1, -10.5) * mm, "end": v(30.14, -10.78) * mm});
            skLineSegment(sketch, "E27.29.0", {"start": v(31.46, -5.94) * mm, "end": v(31.6, -5) * mm});
            skLineSegment(sketch, "E27.29.1", {"start": v(31.75, -4.08) * mm, "end": v(31.6, -5) * mm});
            skLineSegment(sketch, "E27.29.2", {"start": v(29.8, -3.4) * mm, "end": v(31.75, -4.08) * mm});
            skLineSegment(sketch, "E27.29.3", {"start": v(29.4, -5.97) * mm, "end": v(31.46, -5.94) * mm});
            skLineSegment(sketch, "E27.30.0", {"start": v(32, -0.94) * mm, "end": v(32, 0) * mm});
            skLineSegment(sketch, "E27.30.1", {"start": v(32, 0.94) * mm, "end": v(32, 0) * mm});
            skLineSegment(sketch, "E27.30.2", {"start": v(29.97, 1.3) * mm, "end": v(32, 0.94) * mm});
            skLineSegment(sketch, "E27.30.3", {"start": v(29.97, -1.3) * mm, "end": v(32, -0.94) * mm});
            skLineSegment(sketch, "E27.31.0", {"start": v(31.75, 4.08) * mm, "end": v(31.6, 5) * mm});
            skLineSegment(sketch, "E27.31.1", {"start": v(31.46, 5.94) * mm, "end": v(31.6, 5) * mm});
            skLineSegment(sketch, "E27.31.2", {"start": v(29.4, 5.97) * mm, "end": v(31.46, 5.94) * mm});
            skLineSegment(sketch, "E27.31.3", {"start": v(29.8, 3.4) * mm, "end": v(31.75, 4.08) * mm});
            skLineSegment(sketch, "E27.32.0", {"start": v(30.73, 9) * mm, "end": v(30.43, 9.89) * mm});
            skLineSegment(sketch, "E27.32.1", {"start": v(30.14, 10.78) * mm, "end": v(30.43, 9.89) * mm});
            skLineSegment(sketch, "E27.32.2", {"start": v(28.1, 10.5) * mm, "end": v(30.14, 10.78) * mm});
            skLineSegment(sketch, "E27.32.3", {"start": v(28.9, 8.03) * mm, "end": v(30.73, 9) * mm});
            skLineSegment(sketch, "E27.33.0", {"start": v(28.94, 13.69) * mm, "end": v(28.51, 14.53) * mm});
            skLineSegment(sketch, "E27.33.1", {"start": v(28.08, 15.37) * mm, "end": v(28.51, 14.53) * mm});
            skLineSegment(sketch, "E27.33.2", {"start": v(26.11, 14.77) * mm, "end": v(28.08, 15.37) * mm});
            skLineSegment(sketch, "E27.33.3", {"start": v(27.3, 12.45) * mm, "end": v(28.94, 13.69) * mm});
            skLineSegment(sketch, "E27.34.0", {"start": v(26.44, 18.05) * mm, "end": v(25.89, 18.8) * mm});
            skLineSegment(sketch, "E27.34.1", {"start": v(25.33, 19.57) * mm, "end": v(25.89, 18.8) * mm});
            skLineSegment(sketch, "E27.34.2", {"start": v(23.48, 18.67) * mm, "end": v(25.33, 19.57) * mm});
            skLineSegment(sketch, "E27.34.3", {"start": v(25.01, 16.57) * mm, "end": v(26.44, 18.05) * mm});
            skLineSegment(sketch, "E27.35.0", {"start": v(23.3, 21.96) * mm, "end": v(22.63, 22.63) * mm});
            skLineSegment(sketch, "E27.35.1", {"start": v(21.96, 23.3) * mm, "end": v(22.63, 22.63) * mm});
            skLineSegment(sketch, "E27.35.2", {"start": v(20.27, 22.11) * mm, "end": v(21.96, 23.3) * mm});
            skLineSegment(sketch, "E27.35.3", {"start": v(22.11, 20.27) * mm, "end": v(23.3, 21.96) * mm});
            skLineSegment(sketch, "E27.36.0", {"start": v(19.57, 25.33) * mm, "end": v(18.8, 25.89) * mm});
            skLineSegment(sketch, "E27.36.1", {"start": v(18.05, 26.44) * mm, "end": v(18.8, 25.89) * mm});
            skLineSegment(sketch, "E27.36.2", {"start": v(16.57, 25.01) * mm, "end": v(18.05, 26.44) * mm});
            skLineSegment(sketch, "E27.36.3", {"start": v(18.67, 23.48) * mm, "end": v(19.57, 25.33) * mm});
            skLineSegment(sketch, "E27.37.0", {"start": v(15.37, 28.08) * mm, "end": v(14.53, 28.51) * mm});
            skLineSegment(sketch, "E27.37.1", {"start": v(13.69, 28.94) * mm, "end": v(14.53, 28.51) * mm});
            skLineSegment(sketch, "E27.37.2", {"start": v(12.45, 27.3) * mm, "end": v(13.69, 28.94) * mm});
            skLineSegment(sketch, "E27.37.3", {"start": v(14.77, 26.11) * mm, "end": v(15.37, 28.08) * mm});
            skLineSegment(sketch, "E27.38.0", {"start": v(10.78, 30.14) * mm, "end": v(9.89, 30.43) * mm});
            skLineSegment(sketch, "E27.38.1", {"start": v(9, 30.73) * mm, "end": v(9.89, 30.43) * mm});
            skLineSegment(sketch, "E27.38.2", {"start": v(8.03, 28.9) * mm, "end": v(9, 30.73) * mm});
            skLineSegment(sketch, "E27.38.3", {"start": v(10.5, 28.1) * mm, "end": v(10.78, 30.14) * mm});
            skLineSegment(sketch, "E27.39.0", {"start": v(5.94, 31.46) * mm, "end": v(5, 31.6) * mm});
            skLineSegment(sketch, "E27.39.1", {"start": v(4.08, 31.75) * mm, "end": v(5, 31.6) * mm});
            skLineSegment(sketch, "E27.39.2", {"start": v(3.4, 29.8) * mm, "end": v(4.08, 31.75) * mm});
            skLineSegment(sketch, "E27.39.3", {"start": v(5.97, 29.4) * mm, "end": v(5.94, 31.46) * mm});
            skSolve(sketch);
        }
        {
            var Q0;
            Q0 = qSketchRegion(id + "F14", true);
            extrude(context, id + "F15", {"entities" : qUnion([Q0]), "operationType" : NewBodyOperationType.ADD, "depth" : 4 * mm, "offsetDistance" : 25 * mm});
        }
        {
            var Q0;
            Q0=makeQuery(id+"F7.opExtrude","CAP_FACE",FACE,{"disambiguationData":[OSD([sQuery(id+"F0.wireOp",EDGE,"E0")])],"isStart":false});
            var sketch = newSketch(context, id + "F16", { "sketchPlane" : qUnion([Q0])});
            skCircle(sketch, "E28", {"center": v(40, 0) * mm, "radius": 7.5 * mm});
            skLineSegment(sketch, "E29", {"start": v(40, 0) * mm, "end": v(40, 7.5) * mm, "construction": true});
            skLineSegment(sketch, "E30", {"start": v(38.68, 7.38) * mm, "end": v(39.06, 9.5) * mm});
            skLineSegment(sketch, "E31", {"start": v(39.06, 9.5) * mm, "end": v(40.94, 9.5) * mm});
            skLineSegment(sketch, "E32.MirrorCS", {"start": v(41.32, 7.38) * mm, "end": v(40.94, 9.5) * mm});
            skLineSegment(sketch, "E33.1.0", {"start": v(33.65, 7.13) * mm, "end": v(35.18, 8.24) * mm});
            skLineSegment(sketch, "E33.1.1", {"start": v(36.72, 6.75) * mm, "end": v(35.18, 8.24) * mm});
            skLineSegment(sketch, "E33.1.2", {"start": v(34.6, 5.2) * mm, "end": v(33.65, 7.13) * mm});
            skLineSegment(sketch, "E33.2.0", {"start": v(30.67, 2.04) * mm, "end": v(31.26, 3.83) * mm});
            skLineSegment(sketch, "E33.2.1", {"start": v(33.38, 3.53) * mm, "end": v(31.26, 3.83) * mm});
            skLineSegment(sketch, "E33.2.2", {"start": v(32.57, 1.03) * mm, "end": v(30.67, 2.04) * mm});
            skLineSegment(sketch, "E34.1.3.0", {"start": v(31.26, -3.83) * mm, "end": v(30.67, -2.04) * mm});
            skLineSegment(sketch, "E34.3.3.0", {"start": v(32.57, -1.03) * mm, "end": v(30.67, -2.04) * mm});
            skLineSegment(sketch, "E34.6.3.0", {"start": v(33.38, -3.53) * mm, "end": v(31.26, -3.83) * mm});
            skLineSegment(sketch, "E34.1.4.0", {"start": v(35.18, -8.24) * mm, "end": v(33.65, -7.13) * mm});
            skLineSegment(sketch, "E34.3.4.0", {"start": v(34.6, -5.2) * mm, "end": v(33.65, -7.13) * mm});
            skLineSegment(sketch, "E34.6.4.0", {"start": v(36.72, -6.75) * mm, "end": v(35.18, -8.24) * mm});
            skLineSegment(sketch, "E34.1.5.0", {"start": v(40.94, -9.5) * mm, "end": v(39.06, -9.5) * mm});
            skLineSegment(sketch, "E34.3.5.0", {"start": v(38.68, -7.38) * mm, "end": v(39.06, -9.5) * mm});
            skLineSegment(sketch, "E34.6.5.0", {"start": v(41.32, -7.38) * mm, "end": v(40.94, -9.5) * mm});
            skLineSegment(sketch, "E34.1.6.0", {"start": v(46.35, -7.13) * mm, "end": v(44.82, -8.24) * mm});
            skLineSegment(sketch, "E34.3.6.0", {"start": v(43.28, -6.75) * mm, "end": v(44.82, -8.24) * mm});
            skLineSegment(sketch, "E34.6.6.0", {"start": v(45.4, -5.2) * mm, "end": v(46.35, -7.13) * mm});
            skLineSegment(sketch, "E34.1.7.0", {"start": v(49.33, -2.04) * mm, "end": v(48.74, -3.83) * mm});
            skLineSegment(sketch, "E34.3.7.0", {"start": v(46.62, -3.53) * mm, "end": v(48.74, -3.83) * mm});
            skLineSegment(sketch, "E34.6.7.0", {"start": v(47.43, -1.03) * mm, "end": v(49.33, -2.04) * mm});
            skLineSegment(sketch, "E34.1.8.0", {"start": v(48.74, 3.83) * mm, "end": v(49.33, 2.04) * mm});
            skLineSegment(sketch, "E34.3.8.0", {"start": v(47.43, 1.03) * mm, "end": v(49.33, 2.04) * mm});
            skLineSegment(sketch, "E34.6.8.0", {"start": v(46.62, 3.53) * mm, "end": v(48.74, 3.83) * mm});
            skLineSegment(sketch, "E34.1.9.0", {"start": v(44.82, 8.24) * mm, "end": v(46.35, 7.13) * mm});
            skLineSegment(sketch, "E34.3.9.0", {"start": v(45.4, 5.2) * mm, "end": v(46.35, 7.13) * mm});
            skLineSegment(sketch, "E34.6.9.0", {"start": v(43.28, 6.75) * mm, "end": v(44.82, 8.24) * mm});
            skSolve(sketch);
        }
        {
            var Q0;
            Q0 = qSketchRegion(id + "F16", true);
            extrude(context, id + "F17", {"entities" : qUnion([Q0]), "operationType" : NewBodyOperationType.ADD, "depth" : 4 * mm, "offsetDistance" : 25 * mm});
        }
        {
            var Q0;
            Q0=makeQuery(id+"F17.opExtrude","CAP_FACE",FACE,{"disambiguationData":[OSD([sQuery(id+"F16.wireOp",EDGE,"E28"),sQuery(id+"F16.wireOp",EDGE,"E30"),sQuery(id+"F16.wireOp",EDGE,"E31"),sQuery(id+"F16.wireOp",EDGE,"E32.MirrorCS"),sQuery(id+"F16.wireOp",EDGE,"E33.1.0"),sQuery(id+"F16.wireOp",EDGE,"E33.1.1"),sQuery(id+"F16.wireOp",EDGE,"E33.1.2"),sQuery(id+"F16.wireOp",EDGE,"E33.2.0"),sQuery(id+"F16.wireOp",EDGE,"E33.2.1"),sQuery(id+"F16.wireOp",EDGE,"E33.2.2"),sQuery(id+"F16.wireOp",EDGE,"E34.1.3.0"),sQuery(id+"F16.wireOp",EDGE,"E34.3.3.0"),sQuery(id+"F16.wireOp",EDGE,"E34.6.3.0"),sQuery(id+"F16.wireOp",EDGE,"E34.1.4.0"),sQuery(id+"F16.wireOp",EDGE,"E34.3.4.0"),sQuery(id+"F16.wireOp",EDGE,"E34.6.4.0"),sQuery(id+"F16.wireOp",EDGE,"E34.1.5.0"),sQuery(id+"F16.wireOp",EDGE,"E34.3.5.0"),sQuery(id+"F16.wireOp",EDGE,"E34.6.5.0"),sQuery(id+"F16.wireOp",EDGE,"E34.1.6.0"),sQuery(id+"F16.wireOp",EDGE,"E34.3.6.0"),sQuery(id+"F16.wireOp",EDGE,"E34.6.6.0"),sQuery(id+"F16.wireOp",EDGE,"E34.1.7.0"),sQuery(id+"F16.wireOp",EDGE,"E34.3.7.0"),sQuery(id+"F16.wireOp",EDGE,"E34.6.7.0"),sQuery(id+"F16.wireOp",EDGE,"E34.1.8.0"),sQuery(id+"F16.wireOp",EDGE,"E34.3.8.0"),sQuery(id+"F16.wireOp",EDGE,"E34.6.8.0"),sQuery(id+"F16.wireOp",EDGE,"E34.1.9.0"),sQuery(id+"F16.wireOp",EDGE,"E34.3.9.0"),sQuery(id+"F16.wireOp",EDGE,"E34.6.9.0")])],"isStart":false});
            var sketch = newSketch(context, id + "F18", { "sketchPlane" : qUnion([Q0])});
            skCircle(sketch, "E35.0", {"center": v(40, 0) * mm, "radius": 3 * mm});
            skSolve(sketch);
        }
        {
            var Q0;
            Q0 = qSketchRegion(id + "F18", true);
            extrude(context, id + "F19", {"entities" : qUnion([Q0]), "operationType" : NewBodyOperationType.ADD, "depth" : 2 * mm, "offsetDistance" : 25 * mm});
        }
        {
            var Q0;
            Q0=makeQuery(id+"F19.opExtrude","CAP_FACE",FACE,{"disambiguationData":[OSD([sQuery(id+"F18.wireOp",EDGE,"E35.0")])],"isStart":false});
            var sketch = newSketch(context, id + "F20", { "sketchPlane" : qUnion([Q0])});
            skCircle(sketch, "E36", {"center": v(0, 0) * mm, "radius": 98 * mm});
            skCircle(sketch, "E37.0", {"center": v(0, 0) * mm, "radius": 5 * mm});
            skSolve(sketch);
        }
        {
            var Q0;
            Q0 = qSketchRegion(id + "F20", true);
            extrude(context, id + "F21", {"entities" : qUnion([Q0]), "depth" : 1 * mm, "offsetDistance" : 25 * mm});
        }
        {
            var Q0;
            Q0=makeQuery(id+"F21.opExtrude","SWEPT_BODY",BODY,{"disambiguationData":[OSD([sQuery(id+"F20.wireOp",EDGE,"E36"),sQuery(id+"F20.wireOp",EDGE,"E37.0")])]});
            var Q1;
            Q1=makeQuery(id+"F1.opExtrude","SWEPT_BODY",BODY,{"disambiguationData":[OSD([sQuery(id+"F0.wireOp",EDGE,"E0")])]});
            booleanBodies(context, id + "F22", {"operationType" : BooleanOperationType.SUBTRACTION, "tools" : qUnion([Q0]), "targets" : qUnion([Q1]), "keepTools" : true});
        }
        {
            var Q0;
            Q0=makeQuery(id+"F21.opExtrude","CAP_FACE",FACE,{"disambiguationData":[OSD([sQuery(id+"F20.wireOp",EDGE,"E36"),sQuery(id+"F20.wireOp",EDGE,"E37.0")])],"isStart":true});
            var sketch = newSketch(context, id + "F23", { "sketchPlane" : qUnion([Q0])});
            skCircle(sketch, "E38.0", {"center": v(-40, 0) * mm, "radius": 3 * mm});
            skCircle(sketch, "E39", {"center": v(-40, 0) * mm, "radius": 5 * mm});
            skSolve(sketch);
        }
        {
            var Q0;
            Q0 = qSketchRegion(id + "F23", true);
            extrude(context, id + "F24", {"entities" : qUnion([Q0]), "operationType" : NewBodyOperationType.ADD, "endBound" : BoundingType.UP_TO_NEXT, "depth" : 25 * mm, "offsetDistance" : 25 * mm});
        }
        {
            var Q0;
            Q0=makeQuery(id+"F21.opExtrude","CAP_FACE",FACE,{"disambiguationData":[OSD([sQuery(id+"F20.wireOp",EDGE,"E36"),sQuery(id+"F20.wireOp",EDGE,"E37.0")])],"isStart":false});
            var sketch = newSketch(context, id + "F25", { "sketchPlane" : qUnion([Q0])});
            skLineSegment(sketch, "E40.bottom", {"start": v(1.5, 91) * mm, "end": v(-1.5, 91) * mm});
            skLineSegment(sketch, "E40.top", {"start": v(1.5, 71) * mm, "end": v(-1.5, 71) * mm});
            skLineSegment(sketch, "E40.left", {"start": v(1.5, 91) * mm, "end": v(1.5, 71) * mm});
            skLineSegment(sketch, "E40.right", {"start": v(-1.5, 91) * mm, "end": v(-1.5, 71) * mm});
            skPoint(sketch, "E40.middle", {"position": v(0, 81) * mm});
            skLineSegment(sketch, "E41.1.0", {"start": v(-44.2, 79.56) * mm, "end": v(-46.8, 78.06) * mm});
            skLineSegment(sketch, "E41.1.1", {"start": v(-44.2, 79.56) * mm, "end": v(-34.2, 62.24) * mm});
            skLineSegment(sketch, "E41.1.2", {"start": v(-46.8, 78.06) * mm, "end": v(-36.8, 60.74) * mm});
            skLineSegment(sketch, "E41.1.3", {"start": v(-34.2, 62.24) * mm, "end": v(-36.8, 60.74) * mm});
            skLineSegment(sketch, "E41.2.0", {"start": v(-78.06, 46.8) * mm, "end": v(-79.56, 44.2) * mm});
            skLineSegment(sketch, "E41.2.1", {"start": v(-78.06, 46.8) * mm, "end": v(-60.74, 36.8) * mm});
            skLineSegment(sketch, "E41.2.2", {"start": v(-79.56, 44.2) * mm, "end": v(-62.24, 34.2) * mm});
            skLineSegment(sketch, "E41.2.3", {"start": v(-60.74, 36.8) * mm, "end": v(-62.24, 34.2) * mm});
            skLineSegment(sketch, "E41.3.0", {"start": v(-91, 1.5) * mm, "end": v(-91, -1.5) * mm});
            skLineSegment(sketch, "E41.3.1", {"start": v(-91, 1.5) * mm, "end": v(-71, 1.5) * mm});
            skLineSegment(sketch, "E41.3.2", {"start": v(-91, -1.5) * mm, "end": v(-71, -1.5) * mm});
            skLineSegment(sketch, "E41.3.3", {"start": v(-71, 1.5) * mm, "end": v(-71, -1.5) * mm});
            skLineSegment(sketch, "E41.4.0", {"start": v(-79.56, -44.2) * mm, "end": v(-78.06, -46.8) * mm});
            skLineSegment(sketch, "E41.4.1", {"start": v(-79.56, -44.2) * mm, "end": v(-62.24, -34.2) * mm});
            skLineSegment(sketch, "E41.4.2", {"start": v(-78.06, -46.8) * mm, "end": v(-60.74, -36.8) * mm});
            skLineSegment(sketch, "E41.4.3", {"start": v(-62.24, -34.2) * mm, "end": v(-60.74, -36.8) * mm});
            skLineSegment(sketch, "E41.5.0", {"start": v(-46.8, -78.06) * mm, "end": v(-44.2, -79.56) * mm});
            skLineSegment(sketch, "E41.5.1", {"start": v(-46.8, -78.06) * mm, "end": v(-36.8, -60.74) * mm});
            skLineSegment(sketch, "E41.5.2", {"start": v(-44.2, -79.56) * mm, "end": v(-34.2, -62.24) * mm});
            skLineSegment(sketch, "E41.5.3", {"start": v(-36.8, -60.74) * mm, "end": v(-34.2, -62.24) * mm});
            skLineSegment(sketch, "E41.6.0", {"start": v(-1.5, -91) * mm, "end": v(1.5, -91) * mm});
            skLineSegment(sketch, "E41.6.1", {"start": v(-1.5, -91) * mm, "end": v(-1.5, -71) * mm});
            skLineSegment(sketch, "E41.6.2", {"start": v(1.5, -91) * mm, "end": v(1.5, -71) * mm});
            skLineSegment(sketch, "E41.6.3", {"start": v(-1.5, -71) * mm, "end": v(1.5, -71) * mm});
            skLineSegment(sketch, "E41.7.0", {"start": v(44.2, -79.56) * mm, "end": v(46.8, -78.06) * mm});
            skLineSegment(sketch, "E41.7.1", {"start": v(44.2, -79.56) * mm, "end": v(34.2, -62.24) * mm});
            skLineSegment(sketch, "E41.7.2", {"start": v(46.8, -78.06) * mm, "end": v(36.8, -60.74) * mm});
            skLineSegment(sketch, "E41.7.3", {"start": v(34.2, -62.24) * mm, "end": v(36.8, -60.74) * mm});
            skLineSegment(sketch, "E41.8.0", {"start": v(78.06, -46.8) * mm, "end": v(79.56, -44.2) * mm});
            skLineSegment(sketch, "E41.8.1", {"start": v(78.06, -46.8) * mm, "end": v(60.74, -36.8) * mm});
            skLineSegment(sketch, "E41.8.2", {"start": v(79.56, -44.2) * mm, "end": v(62.24, -34.2) * mm});
            skLineSegment(sketch, "E41.8.3", {"start": v(60.74, -36.8) * mm, "end": v(62.24, -34.2) * mm});
            skLineSegment(sketch, "E41.9.0", {"start": v(91, -1.5) * mm, "end": v(91, 1.5) * mm});
            skLineSegment(sketch, "E41.9.1", {"start": v(91, -1.5) * mm, "end": v(71, -1.5) * mm});
            skLineSegment(sketch, "E41.9.2", {"start": v(91, 1.5) * mm, "end": v(71, 1.5) * mm});
            skLineSegment(sketch, "E41.9.3", {"start": v(71, -1.5) * mm, "end": v(71, 1.5) * mm});
            skLineSegment(sketch, "E41.10.0", {"start": v(79.56, 44.2) * mm, "end": v(78.06, 46.8) * mm});
            skLineSegment(sketch, "E41.10.1", {"start": v(79.56, 44.2) * mm, "end": v(62.24, 34.2) * mm});
            skLineSegment(sketch, "E41.10.2", {"start": v(78.06, 46.8) * mm, "end": v(60.74, 36.8) * mm});
            skLineSegment(sketch, "E41.10.3", {"start": v(62.24, 34.2) * mm, "end": v(60.74, 36.8) * mm});
            skLineSegment(sketch, "E41.11.0", {"start": v(46.8, 78.06) * mm, "end": v(44.2, 79.56) * mm});
            skLineSegment(sketch, "E41.11.1", {"start": v(46.8, 78.06) * mm, "end": v(36.8, 60.74) * mm});
            skLineSegment(sketch, "E41.11.2", {"start": v(44.2, 79.56) * mm, "end": v(34.2, 62.24) * mm});
            skLineSegment(sketch, "E41.11.3", {"start": v(36.8, 60.74) * mm, "end": v(34.2, 62.24) * mm});
            skPoint(sketch, "E41.center", {"position": v(0, 0) * mm});
            skSolve(sketch);
        }
        {
            var Q0;
            Q0 = qSketchRegion(id + "F25", true);
            extrude(context, id + "F26", {"entities" : qUnion([Q0]), "operationType" : NewBodyOperationType.REMOVE, "oppositeDirection" : true, "depth" : 0.5 * mm, "offsetDistance" : 25 * mm});
        }
        {
            var Q0;
            Q0=makeQuery(id+"F21.opExtrude","CAP_FACE",FACE,{"disambiguationData":[OSD([sQuery(id+"F20.wireOp",EDGE,"E36"),sQuery(id+"F20.wireOp",EDGE,"E37.0")])],"isStart":false});
            var sketch = newSketch(context, id + "F27", { "sketchPlane" : qUnion([Q0])});
            skLineSegment(sketch, "E42.bottom", {"start": v(0.75, 90.5) * mm, "end": v(-0.75, 90.5) * mm});
            skLineSegment(sketch, "E42.top", {"start": v(0.75, 78.5) * mm, "end": v(-0.75, 78.5) * mm});
            skLineSegment(sketch, "E42.left", {"start": v(0.75, 90.5) * mm, "end": v(0.75, 78.5) * mm});
            skLineSegment(sketch, "E42.right", {"start": v(-0.75, 90.5) * mm, "end": v(-0.75, 78.5) * mm});
            skPoint(sketch, "E42.middle", {"position": v(0, 84.5) * mm});
            skLineSegment(sketch, "E43.1.0", {"start": v(-8.71, 90.08) * mm, "end": v(-10.2, 89.93) * mm});
            skLineSegment(sketch, "E43.1.1", {"start": v(-10.2, 89.93) * mm, "end": v(-8.95, 78) * mm});
            skLineSegment(sketch, "E43.1.2", {"start": v(-8.71, 90.08) * mm, "end": v(-7.46, 78.15) * mm});
            skLineSegment(sketch, "E43.1.3", {"start": v(-7.46, 78.15) * mm, "end": v(-8.95, 78) * mm});
            skLineSegment(sketch, "E43.2.0", {"start": v(-18.08, 88.68) * mm, "end": v(-19.55, 88.37) * mm});
            skLineSegment(sketch, "E43.2.1", {"start": v(-19.55, 88.37) * mm, "end": v(-17.05, 76.63) * mm});
            skLineSegment(sketch, "E43.2.2", {"start": v(-18.08, 88.68) * mm, "end": v(-15.59, 76.94) * mm});
            skLineSegment(sketch, "E43.2.3", {"start": v(-15.59, 76.94) * mm, "end": v(-17.05, 76.63) * mm});
            skLineSegment(sketch, "E43.3.0", {"start": v(-27.25, 86.3) * mm, "end": v(-28.68, 85.84) * mm});
            skLineSegment(sketch, "E43.3.1", {"start": v(-28.68, 85.84) * mm, "end": v(-24.97, 74.43) * mm});
            skLineSegment(sketch, "E43.3.2", {"start": v(-27.25, 86.3) * mm, "end": v(-23.54, 74.89) * mm});
            skLineSegment(sketch, "E43.3.3", {"start": v(-23.54, 74.89) * mm, "end": v(-24.97, 74.43) * mm});
            skLineSegment(sketch, "E43.4.0", {"start": v(-36.12, 82.98) * mm, "end": v(-37.5, 82.37) * mm});
            skLineSegment(sketch, "E43.4.1", {"start": v(-37.5, 82.37) * mm, "end": v(-32.61, 71.4) * mm});
            skLineSegment(sketch, "E43.4.2", {"start": v(-36.12, 82.98) * mm, "end": v(-31.24, 72.02) * mm});
            skLineSegment(sketch, "E43.4.3", {"start": v(-31.24, 72.02) * mm, "end": v(-32.61, 71.4) * mm});
            skLineSegment(sketch, "E43.5.0", {"start": v(-44.6, 78.75) * mm, "end": v(-45.9, 78) * mm});
            skLineSegment(sketch, "E43.5.1", {"start": v(-45.9, 78) * mm, "end": v(-39.9, 67.6) * mm});
            skLineSegment(sketch, "E43.5.2", {"start": v(-44.6, 78.75) * mm, "end": v(-38.6, 68.36) * mm});
            skLineSegment(sketch, "E43.5.3", {"start": v(-38.6, 68.36) * mm, "end": v(-39.9, 67.6) * mm});
            skLineSegment(sketch, "E43.6.0", {"start": v(-52.59, 73.66) * mm, "end": v(-53.8, 72.78) * mm});
            skLineSegment(sketch, "E43.6.1", {"start": v(-53.8, 72.78) * mm, "end": v(-46.75, 63.07) * mm});
            skLineSegment(sketch, "E43.6.2", {"start": v(-52.59, 73.66) * mm, "end": v(-45.53, 63.95) * mm});
            skLineSegment(sketch, "E43.6.3", {"start": v(-45.53, 63.95) * mm, "end": v(-46.75, 63.07) * mm});
            skLineSegment(sketch, "E43.7.0", {"start": v(-60, 67.76) * mm, "end": v(-61.11, 66.75) * mm});
            skLineSegment(sketch, "E43.7.1", {"start": v(-61.11, 66.75) * mm, "end": v(-53.08, 57.84) * mm});
            skLineSegment(sketch, "E43.7.2", {"start": v(-60, 67.76) * mm, "end": v(-51.97, 58.84) * mm});
            skLineSegment(sketch, "E43.7.3", {"start": v(-51.97, 58.84) * mm, "end": v(-53.08, 57.84) * mm});
            skLineSegment(sketch, "E43.8.0", {"start": v(-66.75, 61.11) * mm, "end": v(-67.76, 60) * mm});
            skLineSegment(sketch, "E43.8.1", {"start": v(-67.76, 60) * mm, "end": v(-58.84, 51.97) * mm});
            skLineSegment(sketch, "E43.8.2", {"start": v(-66.75, 61.11) * mm, "end": v(-57.84, 53.08) * mm});
            skLineSegment(sketch, "E43.8.3", {"start": v(-57.84, 53.08) * mm, "end": v(-58.84, 51.97) * mm});
            skLineSegment(sketch, "E43.9.0", {"start": v(-72.78, 53.8) * mm, "end": v(-73.66, 52.59) * mm});
            skLineSegment(sketch, "E43.9.1", {"start": v(-73.66, 52.59) * mm, "end": v(-63.95, 45.53) * mm});
            skLineSegment(sketch, "E43.9.2", {"start": v(-72.78, 53.8) * mm, "end": v(-63.07, 46.75) * mm});
            skLineSegment(sketch, "E43.9.3", {"start": v(-63.07, 46.75) * mm, "end": v(-63.95, 45.53) * mm});
            skLineSegment(sketch, "E43.10.0", {"start": v(-78, 45.9) * mm, "end": v(-78.75, 44.6) * mm});
            skLineSegment(sketch, "E43.10.1", {"start": v(-78.75, 44.6) * mm, "end": v(-68.36, 38.6) * mm});
            skLineSegment(sketch, "E43.10.2", {"start": v(-78, 45.9) * mm, "end": v(-67.6, 39.9) * mm});
            skLineSegment(sketch, "E43.10.3", {"start": v(-67.6, 39.9) * mm, "end": v(-68.36, 38.6) * mm});
            skLineSegment(sketch, "E43.11.0", {"start": v(-82.37, 37.5) * mm, "end": v(-82.98, 36.12) * mm});
            skLineSegment(sketch, "E43.11.1", {"start": v(-82.98, 36.12) * mm, "end": v(-72.02, 31.24) * mm});
            skLineSegment(sketch, "E43.11.2", {"start": v(-82.37, 37.5) * mm, "end": v(-71.4, 32.61) * mm});
            skLineSegment(sketch, "E43.11.3", {"start": v(-71.4, 32.61) * mm, "end": v(-72.02, 31.24) * mm});
            skLineSegment(sketch, "E43.12.0", {"start": v(-85.84, 28.68) * mm, "end": v(-86.3, 27.25) * mm});
            skLineSegment(sketch, "E43.12.1", {"start": v(-86.3, 27.25) * mm, "end": v(-74.89, 23.54) * mm});
            skLineSegment(sketch, "E43.12.2", {"start": v(-85.84, 28.68) * mm, "end": v(-74.43, 24.97) * mm});
            skLineSegment(sketch, "E43.12.3", {"start": v(-74.43, 24.97) * mm, "end": v(-74.89, 23.54) * mm});
            skLineSegment(sketch, "E43.13.0", {"start": v(-88.37, 19.55) * mm, "end": v(-88.68, 18.08) * mm});
            skLineSegment(sketch, "E43.13.1", {"start": v(-88.68, 18.08) * mm, "end": v(-76.94, 15.59) * mm});
            skLineSegment(sketch, "E43.13.2", {"start": v(-88.37, 19.55) * mm, "end": v(-76.63, 17.05) * mm});
            skLineSegment(sketch, "E43.13.3", {"start": v(-76.63, 17.05) * mm, "end": v(-76.94, 15.59) * mm});
            skLineSegment(sketch, "E43.14.0", {"start": v(-89.93, 10.2) * mm, "end": v(-90.08, 8.71) * mm});
            skLineSegment(sketch, "E43.14.1", {"start": v(-90.08, 8.71) * mm, "end": v(-78.15, 7.46) * mm});
            skLineSegment(sketch, "E43.14.2", {"start": v(-89.93, 10.2) * mm, "end": v(-78, 8.95) * mm});
            skLineSegment(sketch, "E43.14.3", {"start": v(-78, 8.95) * mm, "end": v(-78.15, 7.46) * mm});
            skLineSegment(sketch, "E43.15.0", {"start": v(-90.5, 0.75) * mm, "end": v(-90.5, -0.75) * mm});
            skLineSegment(sketch, "E43.15.1", {"start": v(-90.5, -0.75) * mm, "end": v(-78.5, -0.75) * mm});
            skLineSegment(sketch, "E43.15.2", {"start": v(-90.5, 0.75) * mm, "end": v(-78.5, 0.75) * mm});
            skLineSegment(sketch, "E43.15.3", {"start": v(-78.5, 0.75) * mm, "end": v(-78.5, -0.75) * mm});
            skLineSegment(sketch, "E43.16.0", {"start": v(-90.08, -8.71) * mm, "end": v(-89.93, -10.2) * mm});
            skLineSegment(sketch, "E43.16.1", {"start": v(-89.93, -10.2) * mm, "end": v(-78, -8.95) * mm});
            skLineSegment(sketch, "E43.16.2", {"start": v(-90.08, -8.71) * mm, "end": v(-78.15, -7.46) * mm});
            skLineSegment(sketch, "E43.16.3", {"start": v(-78.15, -7.46) * mm, "end": v(-78, -8.95) * mm});
            skLineSegment(sketch, "E43.17.0", {"start": v(-88.68, -18.08) * mm, "end": v(-88.37, -19.55) * mm});
            skLineSegment(sketch, "E43.17.1", {"start": v(-88.37, -19.55) * mm, "end": v(-76.63, -17.05) * mm});
            skLineSegment(sketch, "E43.17.2", {"start": v(-88.68, -18.08) * mm, "end": v(-76.94, -15.59) * mm});
            skLineSegment(sketch, "E43.17.3", {"start": v(-76.94, -15.59) * mm, "end": v(-76.63, -17.05) * mm});
            skLineSegment(sketch, "E43.18.0", {"start": v(-86.3, -27.25) * mm, "end": v(-85.84, -28.68) * mm});
            skLineSegment(sketch, "E43.18.1", {"start": v(-85.84, -28.68) * mm, "end": v(-74.43, -24.97) * mm});
            skLineSegment(sketch, "E43.18.2", {"start": v(-86.3, -27.25) * mm, "end": v(-74.89, -23.54) * mm});
            skLineSegment(sketch, "E43.18.3", {"start": v(-74.89, -23.54) * mm, "end": v(-74.43, -24.97) * mm});
            skLineSegment(sketch, "E43.19.0", {"start": v(-82.98, -36.12) * mm, "end": v(-82.37, -37.5) * mm});
            skLineSegment(sketch, "E43.19.1", {"start": v(-82.37, -37.5) * mm, "end": v(-71.4, -32.61) * mm});
            skLineSegment(sketch, "E43.19.2", {"start": v(-82.98, -36.12) * mm, "end": v(-72.02, -31.24) * mm});
            skLineSegment(sketch, "E43.19.3", {"start": v(-72.02, -31.24) * mm, "end": v(-71.4, -32.61) * mm});
            skLineSegment(sketch, "E43.20.0", {"start": v(-78.75, -44.6) * mm, "end": v(-78, -45.9) * mm});
            skLineSegment(sketch, "E43.20.1", {"start": v(-78, -45.9) * mm, "end": v(-67.6, -39.9) * mm});
            skLineSegment(sketch, "E43.20.2", {"start": v(-78.75, -44.6) * mm, "end": v(-68.36, -38.6) * mm});
            skLineSegment(sketch, "E43.20.3", {"start": v(-68.36, -38.6) * mm, "end": v(-67.6, -39.9) * mm});
            skLineSegment(sketch, "E43.21.0", {"start": v(-73.66, -52.59) * mm, "end": v(-72.78, -53.8) * mm});
            skLineSegment(sketch, "E43.21.1", {"start": v(-72.78, -53.8) * mm, "end": v(-63.07, -46.75) * mm});
            skLineSegment(sketch, "E43.21.2", {"start": v(-73.66, -52.59) * mm, "end": v(-63.95, -45.53) * mm});
            skLineSegment(sketch, "E43.21.3", {"start": v(-63.95, -45.53) * mm, "end": v(-63.07, -46.75) * mm});
            skLineSegment(sketch, "E43.22.0", {"start": v(-67.76, -60) * mm, "end": v(-66.75, -61.11) * mm});
            skLineSegment(sketch, "E43.22.1", {"start": v(-66.75, -61.11) * mm, "end": v(-57.84, -53.08) * mm});
            skLineSegment(sketch, "E43.22.2", {"start": v(-67.76, -60) * mm, "end": v(-58.84, -51.97) * mm});
            skLineSegment(sketch, "E43.22.3", {"start": v(-58.84, -51.97) * mm, "end": v(-57.84, -53.08) * mm});
            skLineSegment(sketch, "E43.23.0", {"start": v(-61.11, -66.75) * mm, "end": v(-60, -67.76) * mm});
            skLineSegment(sketch, "E43.23.1", {"start": v(-60, -67.76) * mm, "end": v(-51.97, -58.84) * mm});
            skLineSegment(sketch, "E43.23.2", {"start": v(-61.11, -66.75) * mm, "end": v(-53.08, -57.84) * mm});
            skLineSegment(sketch, "E43.23.3", {"start": v(-53.08, -57.84) * mm, "end": v(-51.97, -58.84) * mm});
            skLineSegment(sketch, "E43.24.0", {"start": v(-53.8, -72.78) * mm, "end": v(-52.59, -73.66) * mm});
            skLineSegment(sketch, "E43.24.1", {"start": v(-52.59, -73.66) * mm, "end": v(-45.53, -63.95) * mm});
            skLineSegment(sketch, "E43.24.2", {"start": v(-53.8, -72.78) * mm, "end": v(-46.75, -63.07) * mm});
            skLineSegment(sketch, "E43.24.3", {"start": v(-46.75, -63.07) * mm, "end": v(-45.53, -63.95) * mm});
            skLineSegment(sketch, "E43.25.0", {"start": v(-45.9, -78) * mm, "end": v(-44.6, -78.75) * mm});
            skLineSegment(sketch, "E43.25.1", {"start": v(-44.6, -78.75) * mm, "end": v(-38.6, -68.36) * mm});
            skLineSegment(sketch, "E43.25.2", {"start": v(-45.9, -78) * mm, "end": v(-39.9, -67.6) * mm});
            skLineSegment(sketch, "E43.25.3", {"start": v(-39.9, -67.6) * mm, "end": v(-38.6, -68.36) * mm});
            skLineSegment(sketch, "E43.26.0", {"start": v(-37.5, -82.37) * mm, "end": v(-36.12, -82.98) * mm});
            skLineSegment(sketch, "E43.26.1", {"start": v(-36.12, -82.98) * mm, "end": v(-31.24, -72.02) * mm});
            skLineSegment(sketch, "E43.26.2", {"start": v(-37.5, -82.37) * mm, "end": v(-32.61, -71.4) * mm});
            skLineSegment(sketch, "E43.26.3", {"start": v(-32.61, -71.4) * mm, "end": v(-31.24, -72.02) * mm});
            skLineSegment(sketch, "E43.27.0", {"start": v(-28.68, -85.84) * mm, "end": v(-27.25, -86.3) * mm});
            skLineSegment(sketch, "E43.27.1", {"start": v(-27.25, -86.3) * mm, "end": v(-23.54, -74.89) * mm});
            skLineSegment(sketch, "E43.27.2", {"start": v(-28.68, -85.84) * mm, "end": v(-24.97, -74.43) * mm});
            skLineSegment(sketch, "E43.27.3", {"start": v(-24.97, -74.43) * mm, "end": v(-23.54, -74.89) * mm});
            skLineSegment(sketch, "E43.28.0", {"start": v(-19.55, -88.37) * mm, "end": v(-18.08, -88.68) * mm});
            skLineSegment(sketch, "E43.28.1", {"start": v(-18.08, -88.68) * mm, "end": v(-15.59, -76.94) * mm});
            skLineSegment(sketch, "E43.28.2", {"start": v(-19.55, -88.37) * mm, "end": v(-17.05, -76.63) * mm});
            skLineSegment(sketch, "E43.28.3", {"start": v(-17.05, -76.63) * mm, "end": v(-15.59, -76.94) * mm});
            skLineSegment(sketch, "E43.29.0", {"start": v(-10.2, -89.93) * mm, "end": v(-8.71, -90.08) * mm});
            skLineSegment(sketch, "E43.29.1", {"start": v(-8.71, -90.08) * mm, "end": v(-7.46, -78.15) * mm});
            skLineSegment(sketch, "E43.29.2", {"start": v(-10.2, -89.93) * mm, "end": v(-8.95, -78) * mm});
            skLineSegment(sketch, "E43.29.3", {"start": v(-8.95, -78) * mm, "end": v(-7.46, -78.15) * mm});
            skLineSegment(sketch, "E43.30.0", {"start": v(-0.75, -90.5) * mm, "end": v(0.75, -90.5) * mm});
            skLineSegment(sketch, "E43.30.1", {"start": v(0.75, -90.5) * mm, "end": v(0.75, -78.5) * mm});
            skLineSegment(sketch, "E43.30.2", {"start": v(-0.75, -90.5) * mm, "end": v(-0.75, -78.5) * mm});
            skLineSegment(sketch, "E43.30.3", {"start": v(-0.75, -78.5) * mm, "end": v(0.75, -78.5) * mm});
            skLineSegment(sketch, "E43.31.0", {"start": v(8.71, -90.08) * mm, "end": v(10.2, -89.93) * mm});
            skLineSegment(sketch, "E43.31.1", {"start": v(10.2, -89.93) * mm, "end": v(8.95, -78) * mm});
            skLineSegment(sketch, "E43.31.2", {"start": v(8.71, -90.08) * mm, "end": v(7.46, -78.15) * mm});
            skLineSegment(sketch, "E43.31.3", {"start": v(7.46, -78.15) * mm, "end": v(8.95, -78) * mm});
            skLineSegment(sketch, "E43.32.0", {"start": v(18.08, -88.68) * mm, "end": v(19.55, -88.37) * mm});
            skLineSegment(sketch, "E43.32.1", {"start": v(19.55, -88.37) * mm, "end": v(17.05, -76.63) * mm});
            skLineSegment(sketch, "E43.32.2", {"start": v(18.08, -88.68) * mm, "end": v(15.59, -76.94) * mm});
            skLineSegment(sketch, "E43.32.3", {"start": v(15.59, -76.94) * mm, "end": v(17.05, -76.63) * mm});
            skLineSegment(sketch, "E43.33.0", {"start": v(27.25, -86.3) * mm, "end": v(28.68, -85.84) * mm});
            skLineSegment(sketch, "E43.33.1", {"start": v(28.68, -85.84) * mm, "end": v(24.97, -74.43) * mm});
            skLineSegment(sketch, "E43.33.2", {"start": v(27.25, -86.3) * mm, "end": v(23.54, -74.89) * mm});
            skLineSegment(sketch, "E43.33.3", {"start": v(23.54, -74.89) * mm, "end": v(24.97, -74.43) * mm});
            skLineSegment(sketch, "E43.34.0", {"start": v(36.12, -82.98) * mm, "end": v(37.5, -82.37) * mm});
            skLineSegment(sketch, "E43.34.1", {"start": v(37.5, -82.37) * mm, "end": v(32.61, -71.4) * mm});
            skLineSegment(sketch, "E43.34.2", {"start": v(36.12, -82.98) * mm, "end": v(31.24, -72.02) * mm});
            skLineSegment(sketch, "E43.34.3", {"start": v(31.24, -72.02) * mm, "end": v(32.61, -71.4) * mm});
            skLineSegment(sketch, "E43.35.0", {"start": v(44.6, -78.75) * mm, "end": v(45.9, -78) * mm});
            skLineSegment(sketch, "E43.35.1", {"start": v(45.9, -78) * mm, "end": v(39.9, -67.6) * mm});
            skLineSegment(sketch, "E43.35.2", {"start": v(44.6, -78.75) * mm, "end": v(38.6, -68.36) * mm});
            skLineSegment(sketch, "E43.35.3", {"start": v(38.6, -68.36) * mm, "end": v(39.9, -67.6) * mm});
            skLineSegment(sketch, "E43.36.0", {"start": v(52.59, -73.66) * mm, "end": v(53.8, -72.78) * mm});
            skLineSegment(sketch, "E43.36.1", {"start": v(53.8, -72.78) * mm, "end": v(46.75, -63.07) * mm});
            skLineSegment(sketch, "E43.36.2", {"start": v(52.59, -73.66) * mm, "end": v(45.53, -63.95) * mm});
            skLineSegment(sketch, "E43.36.3", {"start": v(45.53, -63.95) * mm, "end": v(46.75, -63.07) * mm});
            skLineSegment(sketch, "E43.37.0", {"start": v(60, -67.76) * mm, "end": v(61.11, -66.75) * mm});
            skLineSegment(sketch, "E43.37.1", {"start": v(61.11, -66.75) * mm, "end": v(53.08, -57.84) * mm});
            skLineSegment(sketch, "E43.37.2", {"start": v(60, -67.76) * mm, "end": v(51.97, -58.84) * mm});
            skLineSegment(sketch, "E43.37.3", {"start": v(51.97, -58.84) * mm, "end": v(53.08, -57.84) * mm});
            skLineSegment(sketch, "E43.38.0", {"start": v(66.75, -61.11) * mm, "end": v(67.76, -60) * mm});
            skLineSegment(sketch, "E43.38.1", {"start": v(67.76, -60) * mm, "end": v(58.84, -51.97) * mm});
            skLineSegment(sketch, "E43.38.2", {"start": v(66.75, -61.11) * mm, "end": v(57.84, -53.08) * mm});
            skLineSegment(sketch, "E43.38.3", {"start": v(57.84, -53.08) * mm, "end": v(58.84, -51.97) * mm});
            skLineSegment(sketch, "E43.39.0", {"start": v(72.78, -53.8) * mm, "end": v(73.66, -52.59) * mm});
            skLineSegment(sketch, "E43.39.1", {"start": v(73.66, -52.59) * mm, "end": v(63.95, -45.53) * mm});
            skLineSegment(sketch, "E43.39.2", {"start": v(72.78, -53.8) * mm, "end": v(63.07, -46.75) * mm});
            skLineSegment(sketch, "E43.39.3", {"start": v(63.07, -46.75) * mm, "end": v(63.95, -45.53) * mm});
            skLineSegment(sketch, "E43.40.0", {"start": v(78, -45.9) * mm, "end": v(78.75, -44.6) * mm});
            skLineSegment(sketch, "E43.40.1", {"start": v(78.75, -44.6) * mm, "end": v(68.36, -38.6) * mm});
            skLineSegment(sketch, "E43.40.2", {"start": v(78, -45.9) * mm, "end": v(67.6, -39.9) * mm});
            skLineSegment(sketch, "E43.40.3", {"start": v(67.6, -39.9) * mm, "end": v(68.36, -38.6) * mm});
            skLineSegment(sketch, "E43.41.0", {"start": v(82.37, -37.5) * mm, "end": v(82.98, -36.12) * mm});
            skLineSegment(sketch, "E43.41.1", {"start": v(82.98, -36.12) * mm, "end": v(72.02, -31.24) * mm});
            skLineSegment(sketch, "E43.41.2", {"start": v(82.37, -37.5) * mm, "end": v(71.4, -32.61) * mm});
            skLineSegment(sketch, "E43.41.3", {"start": v(71.4, -32.61) * mm, "end": v(72.02, -31.24) * mm});
            skLineSegment(sketch, "E43.42.0", {"start": v(85.84, -28.68) * mm, "end": v(86.3, -27.25) * mm});
            skLineSegment(sketch, "E43.42.1", {"start": v(86.3, -27.25) * mm, "end": v(74.89, -23.54) * mm});
            skLineSegment(sketch, "E43.42.2", {"start": v(85.84, -28.68) * mm, "end": v(74.43, -24.97) * mm});
            skLineSegment(sketch, "E43.42.3", {"start": v(74.43, -24.97) * mm, "end": v(74.89, -23.54) * mm});
            skLineSegment(sketch, "E43.43.0", {"start": v(88.37, -19.55) * mm, "end": v(88.68, -18.08) * mm});
            skLineSegment(sketch, "E43.43.1", {"start": v(88.68, -18.08) * mm, "end": v(76.94, -15.59) * mm});
            skLineSegment(sketch, "E43.43.2", {"start": v(88.37, -19.55) * mm, "end": v(76.63, -17.05) * mm});
            skLineSegment(sketch, "E43.43.3", {"start": v(76.63, -17.05) * mm, "end": v(76.94, -15.59) * mm});
            skLineSegment(sketch, "E43.44.0", {"start": v(89.93, -10.2) * mm, "end": v(90.08, -8.71) * mm});
            skLineSegment(sketch, "E43.44.1", {"start": v(90.08, -8.71) * mm, "end": v(78.15, -7.46) * mm});
            skLineSegment(sketch, "E43.44.2", {"start": v(89.93, -10.2) * mm, "end": v(78, -8.95) * mm});
            skLineSegment(sketch, "E43.44.3", {"start": v(78, -8.95) * mm, "end": v(78.15, -7.46) * mm});
            skLineSegment(sketch, "E43.45.0", {"start": v(90.5, -0.75) * mm, "end": v(90.5, 0.75) * mm});
            skLineSegment(sketch, "E43.45.1", {"start": v(90.5, 0.75) * mm, "end": v(78.5, 0.75) * mm});
            skLineSegment(sketch, "E43.45.2", {"start": v(90.5, -0.75) * mm, "end": v(78.5, -0.75) * mm});
            skLineSegment(sketch, "E43.45.3", {"start": v(78.5, -0.75) * mm, "end": v(78.5, 0.75) * mm});
            skLineSegment(sketch, "E43.46.0", {"start": v(90.08, 8.71) * mm, "end": v(89.93, 10.2) * mm});
            skLineSegment(sketch, "E43.46.1", {"start": v(89.93, 10.2) * mm, "end": v(78, 8.95) * mm});
            skLineSegment(sketch, "E43.46.2", {"start": v(90.08, 8.71) * mm, "end": v(78.15, 7.46) * mm});
            skLineSegment(sketch, "E43.46.3", {"start": v(78.15, 7.46) * mm, "end": v(78, 8.95) * mm});
            skLineSegment(sketch, "E43.47.0", {"start": v(88.68, 18.08) * mm, "end": v(88.37, 19.55) * mm});
            skLineSegment(sketch, "E43.47.1", {"start": v(88.37, 19.55) * mm, "end": v(76.63, 17.05) * mm});
            skLineSegment(sketch, "E43.47.2", {"start": v(88.68, 18.08) * mm, "end": v(76.94, 15.59) * mm});
            skLineSegment(sketch, "E43.47.3", {"start": v(76.94, 15.59) * mm, "end": v(76.63, 17.05) * mm});
            skLineSegment(sketch, "E43.48.0", {"start": v(86.3, 27.25) * mm, "end": v(85.84, 28.68) * mm});
            skLineSegment(sketch, "E43.48.1", {"start": v(85.84, 28.68) * mm, "end": v(74.43, 24.97) * mm});
            skLineSegment(sketch, "E43.48.2", {"start": v(86.3, 27.25) * mm, "end": v(74.89, 23.54) * mm});
            skLineSegment(sketch, "E43.48.3", {"start": v(74.89, 23.54) * mm, "end": v(74.43, 24.97) * mm});
            skLineSegment(sketch, "E43.49.0", {"start": v(82.98, 36.12) * mm, "end": v(82.37, 37.5) * mm});
            skLineSegment(sketch, "E43.49.1", {"start": v(82.37, 37.5) * mm, "end": v(71.4, 32.61) * mm});
            skLineSegment(sketch, "E43.49.2", {"start": v(82.98, 36.12) * mm, "end": v(72.02, 31.24) * mm});
            skLineSegment(sketch, "E43.49.3", {"start": v(72.02, 31.24) * mm, "end": v(71.4, 32.61) * mm});
            skLineSegment(sketch, "E43.50.0", {"start": v(78.75, 44.6) * mm, "end": v(78, 45.9) * mm});
            skLineSegment(sketch, "E43.50.1", {"start": v(78, 45.9) * mm, "end": v(67.6, 39.9) * mm});
            skLineSegment(sketch, "E43.50.2", {"start": v(78.75, 44.6) * mm, "end": v(68.36, 38.6) * mm});
            skLineSegment(sketch, "E43.50.3", {"start": v(68.36, 38.6) * mm, "end": v(67.6, 39.9) * mm});
            skLineSegment(sketch, "E43.51.0", {"start": v(73.66, 52.59) * mm, "end": v(72.78, 53.8) * mm});
            skLineSegment(sketch, "E43.51.1", {"start": v(72.78, 53.8) * mm, "end": v(63.07, 46.75) * mm});
            skLineSegment(sketch, "E43.51.2", {"start": v(73.66, 52.59) * mm, "end": v(63.95, 45.53) * mm});
            skLineSegment(sketch, "E43.51.3", {"start": v(63.95, 45.53) * mm, "end": v(63.07, 46.75) * mm});
            skLineSegment(sketch, "E43.52.0", {"start": v(67.76, 60) * mm, "end": v(66.75, 61.11) * mm});
            skLineSegment(sketch, "E43.52.1", {"start": v(66.75, 61.11) * mm, "end": v(57.84, 53.08) * mm});
            skLineSegment(sketch, "E43.52.2", {"start": v(67.76, 60) * mm, "end": v(58.84, 51.97) * mm});
            skLineSegment(sketch, "E43.52.3", {"start": v(58.84, 51.97) * mm, "end": v(57.84, 53.08) * mm});
            skLineSegment(sketch, "E43.53.0", {"start": v(61.11, 66.75) * mm, "end": v(60, 67.76) * mm});
            skLineSegment(sketch, "E43.53.1", {"start": v(60, 67.76) * mm, "end": v(51.97, 58.84) * mm});
            skLineSegment(sketch, "E43.53.2", {"start": v(61.11, 66.75) * mm, "end": v(53.08, 57.84) * mm});
            skLineSegment(sketch, "E43.53.3", {"start": v(53.08, 57.84) * mm, "end": v(51.97, 58.84) * mm});
            skLineSegment(sketch, "E43.54.0", {"start": v(53.8, 72.78) * mm, "end": v(52.59, 73.66) * mm});
            skLineSegment(sketch, "E43.54.1", {"start": v(52.59, 73.66) * mm, "end": v(45.53, 63.95) * mm});
            skLineSegment(sketch, "E43.54.2", {"start": v(53.8, 72.78) * mm, "end": v(46.75, 63.07) * mm});
            skLineSegment(sketch, "E43.54.3", {"start": v(46.75, 63.07) * mm, "end": v(45.53, 63.95) * mm});
            skLineSegment(sketch, "E43.55.0", {"start": v(45.9, 78) * mm, "end": v(44.6, 78.75) * mm});
            skLineSegment(sketch, "E43.55.1", {"start": v(44.6, 78.75) * mm, "end": v(38.6, 68.36) * mm});
            skLineSegment(sketch, "E43.55.2", {"start": v(45.9, 78) * mm, "end": v(39.9, 67.6) * mm});
            skLineSegment(sketch, "E43.55.3", {"start": v(39.9, 67.6) * mm, "end": v(38.6, 68.36) * mm});
            skLineSegment(sketch, "E43.56.0", {"start": v(37.5, 82.37) * mm, "end": v(36.12, 82.98) * mm});
            skLineSegment(sketch, "E43.56.1", {"start": v(36.12, 82.98) * mm, "end": v(31.24, 72.02) * mm});
            skLineSegment(sketch, "E43.56.2", {"start": v(37.5, 82.37) * mm, "end": v(32.61, 71.4) * mm});
            skLineSegment(sketch, "E43.56.3", {"start": v(32.61, 71.4) * mm, "end": v(31.24, 72.02) * mm});
            skLineSegment(sketch, "E43.57.0", {"start": v(28.68, 85.84) * mm, "end": v(27.25, 86.3) * mm});
            skLineSegment(sketch, "E43.57.1", {"start": v(27.25, 86.3) * mm, "end": v(23.54, 74.89) * mm});
            skLineSegment(sketch, "E43.57.2", {"start": v(28.68, 85.84) * mm, "end": v(24.97, 74.43) * mm});
            skLineSegment(sketch, "E43.57.3", {"start": v(24.97, 74.43) * mm, "end": v(23.54, 74.89) * mm});
            skLineSegment(sketch, "E43.58.0", {"start": v(19.55, 88.37) * mm, "end": v(18.08, 88.68) * mm});
            skLineSegment(sketch, "E43.58.1", {"start": v(18.08, 88.68) * mm, "end": v(15.59, 76.94) * mm});
            skLineSegment(sketch, "E43.58.2", {"start": v(19.55, 88.37) * mm, "end": v(17.05, 76.63) * mm});
            skLineSegment(sketch, "E43.58.3", {"start": v(17.05, 76.63) * mm, "end": v(15.59, 76.94) * mm});
            skLineSegment(sketch, "E43.59.0", {"start": v(10.2, 89.93) * mm, "end": v(8.71, 90.08) * mm});
            skLineSegment(sketch, "E43.59.1", {"start": v(8.71, 90.08) * mm, "end": v(7.46, 78.15) * mm});
            skLineSegment(sketch, "E43.59.2", {"start": v(10.2, 89.93) * mm, "end": v(8.95, 78) * mm});
            skLineSegment(sketch, "E43.59.3", {"start": v(8.95, 78) * mm, "end": v(7.46, 78.15) * mm});
            skPoint(sketch, "E43.center", {"position": v(0, 0) * mm});
            skSolve(sketch);
        }
        {
            var Q0;
            Q0 = qSketchRegion(id + "F27", true);
            var Q1;
            Q1 = qConstructionFilter(qBodyType(qCreatedBy(id + "F27" ,EDGE), BodyType.WIRE), ConstructionObject.NO);
            extrude(context, id + "F28", {"entities" : qUnion([Q0]), "operationType" : NewBodyOperationType.REMOVE, "surfaceEntities" : qUnion([Q1]), "oppositeDirection" : true, "depth" : 0.2 * mm, "offsetDistance" : 25 * mm});
        }
        {
            var Q0;
            Q0=makeQuery(id+"F26.boolean.opBoolean","COPY",FACE,{"derivedFrom":makeQuery(id+"F26.opExtrude","CAP_FACE",FACE,{"disambiguationData":[OSD([sQuery(id+"F25.wireOp",EDGE,"E40.bottom"),sQuery(id+"F25.wireOp",EDGE,"E40.top"),sQuery(id+"F25.wireOp",EDGE,"E40.left"),sQuery(id+"F25.wireOp",EDGE,"E40.right")])],"isStart":false})});
            extrude(context, id + "F29", {"entities" : qUnion([Q0]), "depth" : 1 * mm, "offsetDistance" : 25 * mm});
        }
        {
            var Q0;
            Q0=makeQuery(id+"F28.boolean.opBoolean","COPY",FACE,{"derivedFrom":makeQuery(id+"F28.opExtrude","CAP_FACE",FACE,{"disambiguationData":[OSD([sQuery(id+"F27.wireOp",EDGE,"E43.59.0"),sQuery(id+"F27.wireOp",EDGE,"E43.59.1"),sQuery(id+"F27.wireOp",EDGE,"E43.59.2"),sQuery(id+"F27.wireOp",EDGE,"E43.59.3")])],"isStart":false})});
            extrude(context, id + "F30", {"entities" : qUnion([Q0]), "depth" : 0.4 * mm, "offsetDistance" : 25 * mm});
        }
        {
            var Q0;
            Q0=makeQuery(id+"F15.opExtrude","CAP_FACE",FACE,{"disambiguationData":[OSD([sQuery(id+"F14.wireOp",EDGE,"E21.0"),sQuery(id+"F14.wireOp",EDGE,"E22"),sQuery(id+"F14.wireOp",EDGE,"E23"),sQuery(id+"F14.wireOp",EDGE,"E24"),sQuery(id+"F14.wireOp",EDGE,"E25.MirrorCS"),sQuery(id+"F14.wireOp",EDGE,"E26.MirrorCS"),sQuery(id+"F14.wireOp",EDGE,"E27.1.0"),sQuery(id+"F14.wireOp",EDGE,"E27.1.1"),sQuery(id+"F14.wireOp",EDGE,"E27.1.2"),sQuery(id+"F14.wireOp",EDGE,"E27.1.3"),sQuery(id+"F14.wireOp",EDGE,"E27.2.0"),sQuery(id+"F14.wireOp",EDGE,"E27.2.1"),sQuery(id+"F14.wireOp",EDGE,"E27.2.2"),sQuery(id+"F14.wireOp",EDGE,"E27.2.3"),sQuery(id+"F14.wireOp",EDGE,"E27.3.0"),sQuery(id+"F14.wireOp",EDGE,"E27.3.1"),sQuery(id+"F14.wireOp",EDGE,"E27.3.2"),sQuery(id+"F14.wireOp",EDGE,"E27.3.3"),sQuery(id+"F14.wireOp",EDGE,"E27.4.0"),sQuery(id+"F14.wireOp",EDGE,"E27.4.1"),sQuery(id+"F14.wireOp",EDGE,"E27.4.2"),sQuery(id+"F14.wireOp",EDGE,"E27.4.3"),sQuery(id+"F14.wireOp",EDGE,"E27.5.0"),sQuery(id+"F14.wireOp",EDGE,"E27.5.1"),sQuery(id+"F14.wireOp",EDGE,"E27.5.2"),sQuery(id+"F14.wireOp",EDGE,"E27.5.3"),sQuery(id+"F14.wireOp",EDGE,"E27.6.0"),sQuery(id+"F14.wireOp",EDGE,"E27.6.1"),sQuery(id+"F14.wireOp",EDGE,"E27.6.2"),sQuery(id+"F14.wireOp",EDGE,"E27.6.3"),sQuery(id+"F14.wireOp",EDGE,"E27.7.0"),sQuery(id+"F14.wireOp",EDGE,"E27.7.1"),sQuery(id+"F14.wireOp",EDGE,"E27.7.2"),sQuery(id+"F14.wireOp",EDGE,"E27.7.3"),sQuery(id+"F14.wireOp",EDGE,"E27.8.0"),sQuery(id+"F14.wireOp",EDGE,"E27.8.1"),sQuery(id+"F14.wireOp",EDGE,"E27.8.2"),sQuery(id+"F14.wireOp",EDGE,"E27.8.3"),sQuery(id+"F14.wireOp",EDGE,"E27.9.0"),sQuery(id+"F14.wireOp",EDGE,"E27.9.1"),sQuery(id+"F14.wireOp",EDGE,"E27.9.2"),sQuery(id+"F14.wireOp",EDGE,"E27.9.3"),sQuery(id+"F14.wireOp",EDGE,"E27.10.0"),sQuery(id+"F14.wireOp",EDGE,"E27.10.1"),sQuery(id+"F14.wireOp",EDGE,"E27.10.2"),sQuery(id+"F14.wireOp",EDGE,"E27.10.3"),sQuery(id+"F14.wireOp",EDGE,"E27.11.0"),sQuery(id+"F14.wireOp",EDGE,"E27.11.1"),sQuery(id+"F14.wireOp",EDGE,"E27.11.2"),sQuery(id+"F14.wireOp",EDGE,"E27.11.3"),sQuery(id+"F14.wireOp",EDGE,"E27.12.0"),sQuery(id+"F14.wireOp",EDGE,"E27.12.1"),sQuery(id+"F14.wireOp",EDGE,"E27.12.2"),sQuery(id+"F14.wireOp",EDGE,"E27.12.3"),sQuery(id+"F14.wireOp",EDGE,"E27.13.0"),sQuery(id+"F14.wireOp",EDGE,"E27.13.1"),sQuery(id+"F14.wireOp",EDGE,"E27.13.2"),sQuery(id+"F14.wireOp",EDGE,"E27.13.3"),sQuery(id+"F14.wireOp",EDGE,"E27.14.0"),sQuery(id+"F14.wireOp",EDGE,"E27.14.1"),sQuery(id+"F14.wireOp",EDGE,"E27.14.2"),sQuery(id+"F14.wireOp",EDGE,"E27.14.3"),sQuery(id+"F14.wireOp",EDGE,"E27.15.0"),sQuery(id+"F14.wireOp",EDGE,"E27.15.1"),sQuery(id+"F14.wireOp",EDGE,"E27.15.2"),sQuery(id+"F14.wireOp",EDGE,"E27.15.3"),sQuery(id+"F14.wireOp",EDGE,"E27.16.0"),sQuery(id+"F14.wireOp",EDGE,"E27.16.1"),sQuery(id+"F14.wireOp",EDGE,"E27.16.2"),sQuery(id+"F14.wireOp",EDGE,"E27.16.3"),sQuery(id+"F14.wireOp",EDGE,"E27.17.0"),sQuery(id+"F14.wireOp",EDGE,"E27.17.1"),sQuery(id+"F14.wireOp",EDGE,"E27.17.2"),sQuery(id+"F14.wireOp",EDGE,"E27.17.3"),sQuery(id+"F14.wireOp",EDGE,"E27.18.0"),sQuery(id+"F14.wireOp",EDGE,"E27.18.1"),sQuery(id+"F14.wireOp",EDGE,"E27.18.2"),sQuery(id+"F14.wireOp",EDGE,"E27.18.3"),sQuery(id+"F14.wireOp",EDGE,"E27.19.0"),sQuery(id+"F14.wireOp",EDGE,"E27.19.1"),sQuery(id+"F14.wireOp",EDGE,"E27.19.2"),sQuery(id+"F14.wireOp",EDGE,"E27.19.3"),sQuery(id+"F14.wireOp",EDGE,"E27.20.0"),sQuery(id+"F14.wireOp",EDGE,"E27.20.1"),sQuery(id+"F14.wireOp",EDGE,"E27.20.2"),sQuery(id+"F14.wireOp",EDGE,"E27.20.3"),sQuery(id+"F14.wireOp",EDGE,"E27.21.0"),sQuery(id+"F14.wireOp",EDGE,"E27.21.1"),sQuery(id+"F14.wireOp",EDGE,"E27.21.2"),sQuery(id+"F14.wireOp",EDGE,"E27.21.3"),sQuery(id+"F14.wireOp",EDGE,"E27.22.0"),sQuery(id+"F14.wireOp",EDGE,"E27.22.1"),sQuery(id+"F14.wireOp",EDGE,"E27.22.2"),sQuery(id+"F14.wireOp",EDGE,"E27.22.3"),sQuery(id+"F14.wireOp",EDGE,"E27.23.0"),sQuery(id+"F14.wireOp",EDGE,"E27.23.1"),sQuery(id+"F14.wireOp",EDGE,"E27.23.2"),sQuery(id+"F14.wireOp",EDGE,"E27.23.3"),sQuery(id+"F14.wireOp",EDGE,"E27.24.0"),sQuery(id+"F14.wireOp",EDGE,"E27.24.1"),sQuery(id+"F14.wireOp",EDGE,"E27.24.2"),sQuery(id+"F14.wireOp",EDGE,"E27.24.3"),sQuery(id+"F14.wireOp",EDGE,"E27.25.0"),sQuery(id+"F14.wireOp",EDGE,"E27.25.1"),sQuery(id+"F14.wireOp",EDGE,"E27.25.2"),sQuery(id+"F14.wireOp",EDGE,"E27.25.3"),sQuery(id+"F14.wireOp",EDGE,"E27.26.0"),sQuery(id+"F14.wireOp",EDGE,"E27.26.1"),sQuery(id+"F14.wireOp",EDGE,"E27.26.2"),sQuery(id+"F14.wireOp",EDGE,"E27.26.3"),sQuery(id+"F14.wireOp",EDGE,"E27.27.0"),sQuery(id+"F14.wireOp",EDGE,"E27.27.1"),sQuery(id+"F14.wireOp",EDGE,"E27.27.2"),sQuery(id+"F14.wireOp",EDGE,"E27.27.3"),sQuery(id+"F14.wireOp",EDGE,"E27.28.0"),sQuery(id+"F14.wireOp",EDGE,"E27.28.1"),sQuery(id+"F14.wireOp",EDGE,"E27.28.2"),sQuery(id+"F14.wireOp",EDGE,"E27.28.3"),sQuery(id+"F14.wireOp",EDGE,"E27.29.0"),sQuery(id+"F14.wireOp",EDGE,"E27.29.1"),sQuery(id+"F14.wireOp",EDGE,"E27.29.2"),sQuery(id+"F14.wireOp",EDGE,"E27.29.3"),sQuery(id+"F14.wireOp",EDGE,"E27.30.0"),sQuery(id+"F14.wireOp",EDGE,"E27.30.1"),sQuery(id+"F14.wireOp",EDGE,"E27.30.2"),sQuery(id+"F14.wireOp",EDGE,"E27.30.3"),sQuery(id+"F14.wireOp",EDGE,"E27.31.0"),sQuery(id+"F14.wireOp",EDGE,"E27.31.1"),sQuery(id+"F14.wireOp",EDGE,"E27.31.2"),sQuery(id+"F14.wireOp",EDGE,"E27.31.3"),sQuery(id+"F14.wireOp",EDGE,"E27.32.0"),sQuery(id+"F14.wireOp",EDGE,"E27.32.1"),sQuery(id+"F14.wireOp",EDGE,"E27.32.2"),sQuery(id+"F14.wireOp",EDGE,"E27.32.3"),sQuery(id+"F14.wireOp",EDGE,"E27.33.0"),sQuery(id+"F14.wireOp",EDGE,"E27.33.1"),sQuery(id+"F14.wireOp",EDGE,"E27.33.2"),sQuery(id+"F14.wireOp",EDGE,"E27.33.3"),sQuery(id+"F14.wireOp",EDGE,"E27.34.0"),sQuery(id+"F14.wireOp",EDGE,"E27.34.1"),sQuery(id+"F14.wireOp",EDGE,"E27.34.2"),sQuery(id+"F14.wireOp",EDGE,"E27.34.3"),sQuery(id+"F14.wireOp",EDGE,"E27.35.0"),sQuery(id+"F14.wireOp",EDGE,"E27.35.1"),sQuery(id+"F14.wireOp",EDGE,"E27.35.2"),sQuery(id+"F14.wireOp",EDGE,"E27.35.3"),sQuery(id+"F14.wireOp",EDGE,"E27.36.0"),sQuery(id+"F14.wireOp",EDGE,"E27.36.1"),sQuery(id+"F14.wireOp",EDGE,"E27.36.2"),sQuery(id+"F14.wireOp",EDGE,"E27.36.3"),sQuery(id+"F14.wireOp",EDGE,"E27.37.0"),sQuery(id+"F14.wireOp",EDGE,"E27.37.1"),sQuery(id+"F14.wireOp",EDGE,"E27.37.2"),sQuery(id+"F14.wireOp",EDGE,"E27.37.3"),sQuery(id+"F14.wireOp",EDGE,"E27.38.0"),sQuery(id+"F14.wireOp",EDGE,"E27.38.1"),sQuery(id+"F14.wireOp",EDGE,"E27.38.2"),sQuery(id+"F14.wireOp",EDGE,"E27.38.3"),sQuery(id+"F14.wireOp",EDGE,"E27.39.0"),sQuery(id+"F14.wireOp",EDGE,"E27.39.1"),sQuery(id+"F14.wireOp",EDGE,"E27.39.2"),sQuery(id+"F14.wireOp",EDGE,"E27.39.3")])],"isStart":false});
            var sketch = newSketch(context, id + "F31", { "sketchPlane" : qUnion([Q0])});
            skCircle(sketch, "E44.0", {"center": v(0, 0) * mm, "radius": 3 * mm});
            skCircle(sketch, "E45.0", {"center": v(0, 0) * mm, "radius": 5 * mm});
            skSolve(sketch);
        }
        {
            var Q0;
            Q0 = qSketchRegion(id + "F31", true);
            extrude(context, id + "F32", {"entities" : qUnion([Q0]), "operationType" : NewBodyOperationType.ADD, "depth" : 5 * mm, "offsetDistance" : 25 * mm});
        }
        {
            var Q0;
            Q0=makeQuery(id+"F32.opExtrude","CAP_FACE",FACE,{"disambiguationData":[OSD([sQuery(id+"F31.wireOp",EDGE,"E44.0"),sQuery(id+"F31.wireOp",EDGE,"E45.0")])],"isStart":false});
            var sketch = newSketch(context, id + "F33", { "sketchPlane" : qUnion([Q0])});
            skCircle(sketch, "E46.0", {"center": v(0, 0) * mm, "radius": 3 * mm});
            skCircle(sketch, "E47.0", {"center": v(0, 0) * mm, "radius": 5 * mm});
            skLineSegment(sketch, "E48", {"start": v(3, 4) * mm, "end": v(1.5, 50) * mm});
            skLineSegment(sketch, "E49", {"start": v(1.5, 50) * mm, "end": v(0, 50) * mm});
            skLineSegment(sketch, "E50.MirrorCS", {"start": v(-1.5, 50) * mm, "end": v(0, 50) * mm});
            skLineSegment(sketch, "E51.MirrorCS", {"start": v(-3, 4) * mm, "end": v(-1.5, 50) * mm});
            skSolve(sketch);
        }
        {
            var Q0;
            Q0 = qSketchRegion(id + "F33", true);
            extrude(context, id + "F34", {"entities" : qUnion([Q0]), "operationType" : NewBodyOperationType.ADD, "depth" : 1 * mm, "offsetDistance" : 25 * mm});
        }
        {
            var Q0;
            Q0=makeQuery(id+"F6.opExtrude","CAP_FACE",FACE,{"disambiguationData":[OSD([sQuery(id+"F0.wireOp",EDGE,"E0")])],"isStart":false});
            var sketch = newSketch(context, id + "F35", { "sketchPlane" : qUnion([Q0])});
            skCircle(sketch, "E52", {"center": v(0, 0) * mm, "radius": 5 * mm});
            skLineSegment(sketch, "E53", {"start": v(2, 4.58) * mm, "end": v(0.5, 80) * mm});
            skLineSegment(sketch, "E54", {"start": v(0.5, 80) * mm, "end": v(0, 80) * mm});
            skLineSegment(sketch, "E55.MirrorCS", {"start": v(-0.5, 80) * mm, "end": v(0, 80) * mm});
            skLineSegment(sketch, "E56.MirrorCS", {"start": v(-2, 4.58) * mm, "end": v(-0.5, 80) * mm});
            skSolve(sketch);
        }
        {
            var Q0;
            Q0 = qSketchRegion(id + "F35", true);
            extrude(context, id + "F36", {"entities" : qUnion([Q0]), "operationType" : NewBodyOperationType.ADD, "oppositeDirection" : true, "depth" : 1 * mm, "offsetDistance" : 25 * mm});
        }
    });
